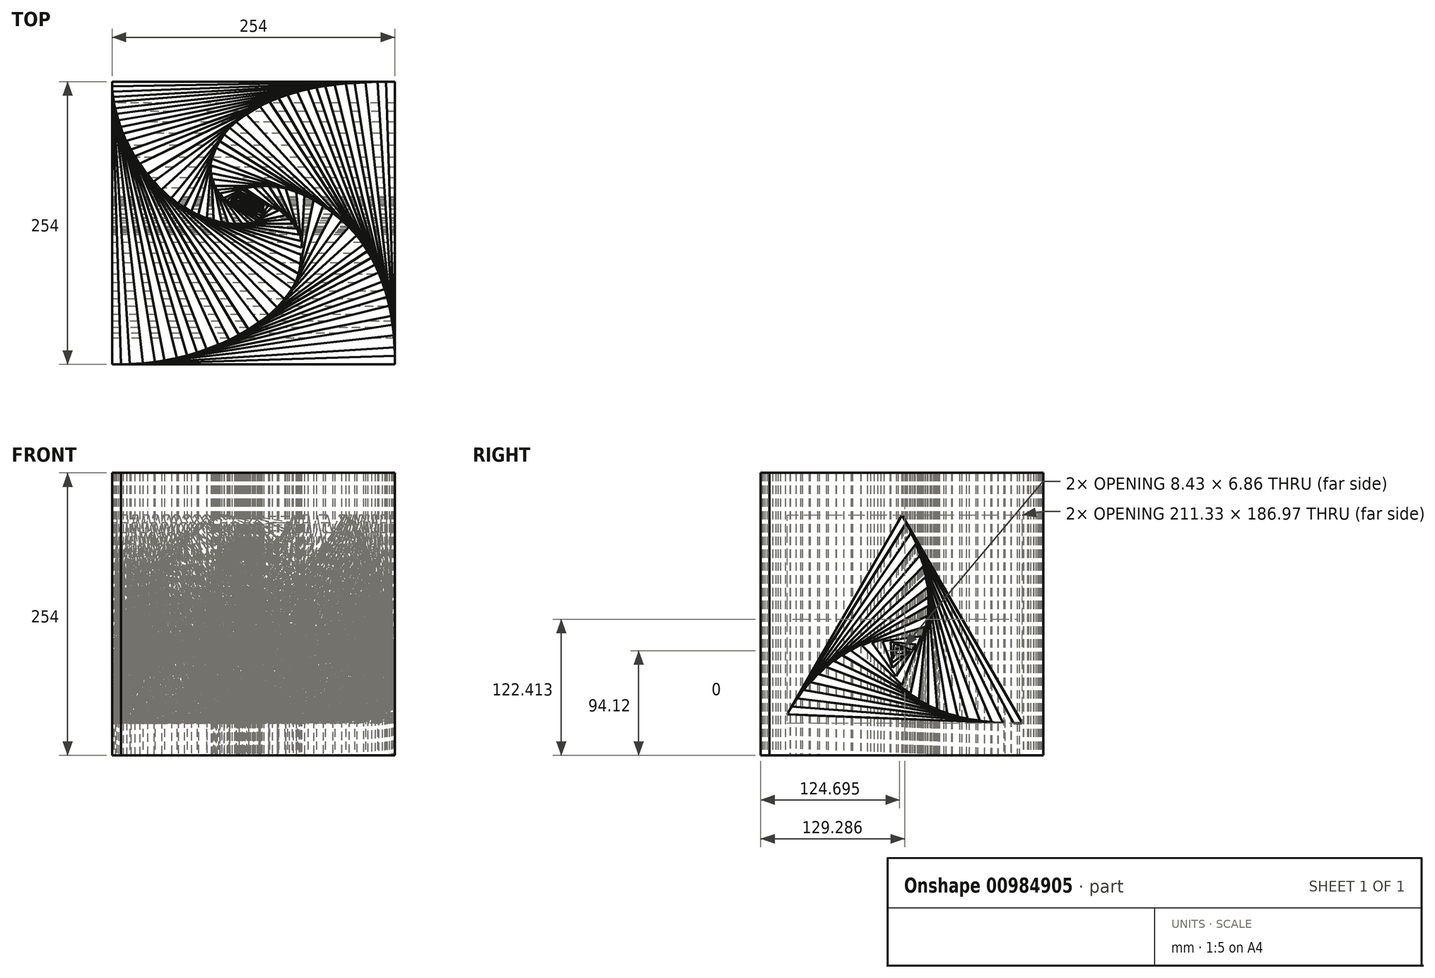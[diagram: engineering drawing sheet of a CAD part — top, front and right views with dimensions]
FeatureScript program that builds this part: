
annotation { "Feature Type Name" : "Feature", "Feature Type Description" : "" }
export const myFeature = defineFeature(function(context is Context, id is Id, definition is map)
    precondition{}
    {
        {
            var Q0;
            Q0=qCreatedBy(makeId("Top.planeOp"),FACE);
            var sketch = newSketch(context, id + "F0", { "sketchPlane" : qUnion([Q0])});
            skLineSegment(sketch, "E0.bottom", {"start": v(-127, 127) * mm, "end": v(127, 127) * mm});
            skLineSegment(sketch, "E0.top", {"start": v(-127, -127) * mm, "end": v(127, -127) * mm});
            skLineSegment(sketch, "E0.left", {"start": v(-127, 127) * mm, "end": v(-127, -127) * mm});
            skLineSegment(sketch, "E0.right", {"start": v(127, 127) * mm, "end": v(127, -127) * mm});
            skPoint(sketch, "E0.middle", {"position": v(0, 0) * mm});
            skLineSegment(sketch, "E1", {"start": v(-127, 127) * mm, "end": v(-119.05, -127) * mm});
            skLineSegment(sketch, "E2", {"start": v(-119.05, -127) * mm, "end": v(127, -119.3) * mm});
            skLineSegment(sketch, "E3", {"start": v(127, -119.3) * mm, "end": v(119.3, 127) * mm});
            skLineSegment(sketch, "E4", {"start": v(119.3, 127) * mm, "end": v(-126.87, 122.79) * mm});
            skLineSegment(sketch, "E5", {"start": v(-126.87, 122.79) * mm, "end": v(-111, -126.75) * mm});
            skLineSegment(sketch, "E6", {"start": v(-111, -126.75) * mm, "end": v(126.76, -111.62) * mm});
            skLineSegment(sketch, "E7", {"start": v(126.76, -111.62) * mm, "end": v(111.59, 126.87) * mm});
            skLineSegment(sketch, "E8", {"start": v(111.59, 126.87) * mm, "end": v(-126.58, 118.23) * mm});
            skLineSegment(sketch, "E9", {"start": v(-126.58, 118.23) * mm, "end": v(-99.33, -126) * mm});
            skLineSegment(sketch, "E10", {"start": v(-99.33, -126) * mm, "end": v(126.07, -100.86) * mm});
            skLineSegment(sketch, "E11", {"start": v(126.07, -100.86) * mm, "end": v(100.71, 126.47) * mm});
            skLineSegment(sketch, "E12", {"start": v(100.71, 126.47) * mm, "end": v(-126.05, 113.53) * mm});
            skLineSegment(sketch, "E13", {"start": v(-126.05, 113.53) * mm, "end": v(-88.65, -124.81) * mm});
            skLineSegment(sketch, "E14", {"start": v(-88.65, -124.81) * mm, "end": v(125, -91.28) * mm});
            skLineSegment(sketch, "E15", {"start": v(125, -91.28) * mm, "end": v(90.92, 125.91) * mm});
            skLineSegment(sketch, "E16", {"start": v(90.92, 125.91) * mm, "end": v(-125.33, 108.92) * mm});
            skLineSegment(sketch, "E17", {"start": v(-125.33, 108.92) * mm, "end": v(-79.79, -123.42) * mm});
            skLineSegment(sketch, "E18", {"start": v(-79.79, -123.42) * mm, "end": v(123.79, -83.52) * mm});
            skLineSegment(sketch, "E19", {"start": v(123.79, -83.52) * mm, "end": v(82.86, 125.28) * mm});
            skLineSegment(sketch, "E20", {"start": v(82.86, 125.28) * mm, "end": v(-124.22, 103.24) * mm});
            skLineSegment(sketch, "E21", {"start": v(-124.22, 103.24) * mm, "end": v(-68.88, -121.29) * mm});
            skLineSegment(sketch, "E22", {"start": v(-68.88, -121.29) * mm, "end": v(121.97, -74.25) * mm});
            skLineSegment(sketch, "E23", {"start": v(121.97, -74.25) * mm, "end": v(73.06, 124.24) * mm});
            skLineSegment(sketch, "E24", {"start": v(73.06, 124.24) * mm, "end": v(-122.95, 98.1) * mm});
            skLineSegment(sketch, "E25", {"start": v(-122.95, 98.1) * mm, "end": v(-59.5, -118.98) * mm});
            skLineSegment(sketch, "E26", {"start": v(-59.5, -118.98) * mm, "end": v(120.06, -66.5) * mm});
            skLineSegment(sketch, "E27", {"start": v(120.06, -66.5) * mm, "end": v(64.65, 123.12) * mm});
            skLineSegment(sketch, "E28", {"start": v(64.65, 123.12) * mm, "end": v(-121.26, 92.3) * mm});
            skLineSegment(sketch, "E29", {"start": v(-121.26, 92.3) * mm, "end": v(-50.64, -116.38) * mm});
            skLineSegment(sketch, "E30", {"start": v(-50.64, -116.38) * mm, "end": v(117.97, -59.33) * mm});
            skLineSegment(sketch, "E31", {"start": v(117.97, -59.33) * mm, "end": v(56.68, 121.8) * mm});
            skLineSegment(sketch, "E32", {"start": v(56.68, 121.8) * mm, "end": v(-119.2, 86.25) * mm});
            skLineSegment(sketch, "E33", {"start": v(-119.2, 86.25) * mm, "end": v(-42.07, -113.48) * mm});
            skLineSegment(sketch, "E34", {"start": v(-42.07, -113.48) * mm, "end": v(115.68, -52.56) * mm});
            skLineSegment(sketch, "E35", {"start": v(115.68, -52.56) * mm, "end": v(48.94, 120.23) * mm});
            skLineSegment(sketch, "E36", {"start": v(48.94, 120.23) * mm, "end": v(-116.98, 80.48) * mm});
            skLineSegment(sketch, "E37", {"start": v(-116.98, 80.48) * mm, "end": v(-31.49, -109.4) * mm});
            skLineSegment(sketch, "E38", {"start": v(-31.49, -109.4) * mm, "end": v(112.58, -44.53) * mm});
            skLineSegment(sketch, "E39", {"start": v(112.58, -44.53) * mm, "end": v(39.42, 117.95) * mm});
            skLineSegment(sketch, "E40", {"start": v(39.42, 117.95) * mm, "end": v(-114.03, 73.93) * mm});
            skLineSegment(sketch, "E41", {"start": v(-114.03, 73.93) * mm, "end": v(-21.72, -105) * mm});
            skLineSegment(sketch, "E42", {"start": v(-21.72, -105) * mm, "end": v(109.35, -37.38) * mm});
            skLineSegment(sketch, "E43", {"start": v(109.35, -37.38) * mm, "end": v(30.54, 115.4) * mm});
            skLineSegment(sketch, "E44", {"start": v(30.54, 115.4) * mm, "end": v(-110.01, 66.14) * mm});
            skLineSegment(sketch, "E45", {"start": v(-110.01, 66.14) * mm, "end": v(-12.99, -100.5) * mm});
            skLineSegment(sketch, "E46", {"start": v(-12.99, -100.5) * mm, "end": v(106.13, -31.13) * mm});
            skLineSegment(sketch, "E47", {"start": v(106.13, -31.13) * mm, "end": v(22.46, 112.57) * mm});
            skLineSegment(sketch, "E48", {"start": v(22.46, 112.57) * mm, "end": v(-106.49, 60.09) * mm});
            skLineSegment(sketch, "E49", {"start": v(-106.49, 60.09) * mm, "end": v(-4.22, -95.4) * mm});
            skLineSegment(sketch, "E50", {"start": v(-4.22, -95.4) * mm, "end": v(102.63, -25.11) * mm});
            skLineSegment(sketch, "E51", {"start": v(102.63, -25.11) * mm, "end": v(14.26, 109.24) * mm});
            skLineSegment(sketch, "E52", {"start": v(14.26, 109.24) * mm, "end": v(-102.15, 53.5) * mm});
            skLineSegment(sketch, "E53", {"start": v(-102.15, 53.5) * mm, "end": v(4.72, -89.5) * mm});
            skLineSegment(sketch, "E54", {"start": v(4.72, -89.5) * mm, "end": v(98.76, -19.23) * mm});
            skLineSegment(sketch, "E55", {"start": v(98.76, -19.23) * mm, "end": v(5.78, 105.18) * mm});
            skLineSegment(sketch, "E56", {"start": v(5.78, 105.18) * mm, "end": v(-95.2, 44.2) * mm});
            skLineSegment(sketch, "E57", {"start": v(-95.2, 44.2) * mm, "end": v(13.74, -82.77) * mm});
            skLineSegment(sketch, "E58", {"start": v(13.74, -82.77) * mm, "end": v(92.63, -11.03) * mm});
            skLineSegment(sketch, "E59", {"start": v(92.63, -11.03) * mm, "end": v(-6.37, 97.84) * mm});
            skLineSegment(sketch, "E60", {"start": v(-6.37, 97.84) * mm, "end": v(-89.35, 37.38) * mm});
            skLineSegment(sketch, "E61", {"start": v(-89.35, 37.38) * mm, "end": v(21.24, -75.94) * mm});
            skLineSegment(sketch, "E62", {"start": v(21.24, -75.94) * mm, "end": v(85.78, -3.5) * mm});
            skLineSegment(sketch, "E63", {"start": v(85.78, -3.5) * mm, "end": v(-15.42, 91.25) * mm});
            skLineSegment(sketch, "E64", {"start": v(-15.42, 91.25) * mm, "end": v(-82.44, 30.3) * mm});
            skLineSegment(sketch, "E65", {"start": v(-82.44, 30.3) * mm, "end": v(28.14, -68.2) * mm});
            skLineSegment(sketch, "E66", {"start": v(28.14, -68.2) * mm, "end": v(79.25, 2.62) * mm});
            skLineSegment(sketch, "E67", {"start": v(79.25, 2.62) * mm, "end": v(-21.42, 85.8) * mm});
            skLineSegment(sketch, "E68", {"start": v(-21.42, 85.8) * mm, "end": v(-73.7, 22.51) * mm});
            skLineSegment(sketch, "E69", {"start": v(-73.7, 22.51) * mm, "end": v(34.67, -59.15) * mm});
            skLineSegment(sketch, "E70", {"start": v(34.67, -59.15) * mm, "end": v(71.24, 9.23) * mm});
            skLineSegment(sketch, "E71", {"start": v(71.24, 9.23) * mm, "end": v(-26.43, 79.72) * mm});
            skLineSegment(sketch, "E72", {"start": v(-26.43, 79.72) * mm, "end": v(-67.61, 17.93) * mm});
            skLineSegment(sketch, "E73", {"start": v(-67.61, 17.93) * mm, "end": v(38.19, -52.58) * mm});
            skLineSegment(sketch, "E74", {"start": v(38.19, -52.58) * mm, "end": v(62.66, 15.43) * mm});
            skLineSegment(sketch, "E75", {"start": v(62.66, 15.43) * mm, "end": v(-30.38, 73.8) * mm});
            skLineSegment(sketch, "E76", {"start": v(-30.38, 73.8) * mm, "end": v(-62.2, 14.31) * mm});
            skLineSegment(sketch, "E77", {"start": v(-62.2, 14.31) * mm, "end": v(40.64, -45.77) * mm});
            skLineSegment(sketch, "E78", {"start": v(40.64, -45.77) * mm, "end": v(53.91, 20.91) * mm});
            skLineSegment(sketch, "E79", {"start": v(53.91, 20.91) * mm, "end": v(-33.63, 67.73) * mm});
            skLineSegment(sketch, "E80", {"start": v(-33.63, 67.73) * mm, "end": v(-55.9, 10.64) * mm});
            skLineSegment(sketch, "E81", {"start": v(-55.9, 10.64) * mm, "end": v(42.4, -36.95) * mm});
            skLineSegment(sketch, "E82", {"start": v(42.4, -36.95) * mm, "end": v(45.79, 25.26) * mm});
            skLineSegment(sketch, "E83", {"start": v(45.79, 25.26) * mm, "end": v(-37.51, 57.77) * mm});
            skLineSegment(sketch, "E84", {"start": v(-37.51, 57.77) * mm, "end": v(-49.59, 7.58) * mm});
            skLineSegment(sketch, "E85", {"start": v(-49.59, 7.58) * mm, "end": v(42.85, -28.5) * mm});
            skLineSegment(sketch, "E86", {"start": v(-37.51, 57.77) * mm, "end": v(-41.95, 4.6) * mm});
            skLineSegment(sketch, "E87", {"start": v(-41.95, 4.6) * mm, "end": v(43.2, -22.06) * mm});
            skLineSegment(sketch, "E88", {"start": v(43.2, -22.06) * mm, "end": v(38.47, 28.12) * mm});
            skLineSegment(sketch, "E89", {"start": v(38.47, 28.12) * mm, "end": v(-38.03, 51.63) * mm});
            skLineSegment(sketch, "E90", {"start": v(-38.03, 51.63) * mm, "end": v(-35.88, 2.7) * mm});
            skLineSegment(sketch, "E91", {"start": v(-35.88, 2.7) * mm, "end": v(42.65, -16.2) * mm});
            skLineSegment(sketch, "E92", {"start": v(42.65, -16.2) * mm, "end": v(29.11, 31) * mm});
            skLineSegment(sketch, "E93", {"start": v(29.11, 31) * mm, "end": v(-37.73, 44.93) * mm});
            skLineSegment(sketch, "E94", {"start": v(-37.73, 44.93) * mm, "end": v(-28.57, 0.94) * mm});
            skLineSegment(sketch, "E95", {"start": v(-28.57, 0.94) * mm, "end": v(40.96, -10.3) * mm});
            skLineSegment(sketch, "E96", {"start": v(40.96, -10.3) * mm, "end": v(21.45, 32.59) * mm});
            skLineSegment(sketch, "E97", {"start": v(21.45, 32.59) * mm, "end": v(-36.55, 39.26) * mm});
            skLineSegment(sketch, "E98", {"start": v(-36.55, 39.26) * mm, "end": v(-22.76, 0) * mm});
            skLineSegment(sketch, "E99", {"start": v(-22.76, 0) * mm, "end": v(38.6, -5.12) * mm});
            skLineSegment(sketch, "E100", {"start": v(38.6, -5.12) * mm, "end": v(13.87, 33.46) * mm});
            skLineSegment(sketch, "E101", {"start": v(13.87, 33.46) * mm, "end": v(-34.51, 33.46) * mm});
            skLineSegment(sketch, "E102", {"start": v(-34.51, 33.46) * mm, "end": v(-16.37, -0.53) * mm});
            skLineSegment(sketch, "E103", {"start": v(-16.37, -0.53) * mm, "end": v(35.66, -0.53) * mm});
            skLineSegment(sketch, "E104", {"start": v(35.66, -0.53) * mm, "end": v(6.5, 33.46) * mm});
            skLineSegment(sketch, "E105", {"start": v(6.5, 33.46) * mm, "end": v(-32.55, 29.77) * mm});
            skLineSegment(sketch, "E106", {"start": v(-32.55, 29.77) * mm, "end": v(-10.06, -0.53) * mm});
            skLineSegment(sketch, "E107", {"start": v(-10.06, -0.53) * mm, "end": v(32.23, 3.46) * mm});
            skLineSegment(sketch, "E108", {"start": v(32.23, 3.46) * mm, "end": v(0, 32.85) * mm});
            skLineSegment(sketch, "E109", {"start": v(0, 32.85) * mm, "end": v(-30.16, 26.56) * mm});
            skLineSegment(sketch, "E110", {"start": v(-30.16, 26.56) * mm, "end": v(-4.43, 0) * mm});
            skLineSegment(sketch, "E111", {"start": v(-4.43, 0) * mm, "end": v(28.5, 6.86) * mm});
            skLineSegment(sketch, "E112", {"start": v(28.5, 6.86) * mm, "end": v(-7.55, 31.28) * mm});
            skPoint(sketch, "E112.endSnap0", {"position": v(-7.55, 35.92) * mm});
            skLineSegment(sketch, "E113", {"start": v(-7.55, 31.28) * mm, "end": v(-26.42, 22.7) * mm});
            skLineSegment(sketch, "E114", {"start": v(-26.42, 22.7) * mm, "end": v(0, 0.92) * mm});
            skLineSegment(sketch, "E115", {"start": v(0, 0.92) * mm, "end": v(22.3, 11.06) * mm});
            skLineSegment(sketch, "E116", {"start": v(22.3, 11.06) * mm, "end": v(-10.15, 30.1) * mm});
            skLineSegment(sketch, "E117", {"start": v(-10.15, 30.1) * mm, "end": v(-23.64, 20.4) * mm});
            skLineSegment(sketch, "E118", {"start": v(-23.64, 20.4) * mm, "end": v(3.33, 2.44) * mm});
            skLineSegment(sketch, "E119", {"start": v(3.33, 2.44) * mm, "end": v(17, 14.17) * mm});
            skLineSegment(sketch, "E120", {"start": v(17, 14.17) * mm, "end": v(-12.61, 28.32) * mm});
            skLineSegment(sketch, "E121", {"start": v(-12.61, 28.32) * mm, "end": v(-21.27, 18.83) * mm});
            skLineSegment(sketch, "E122", {"start": v(-21.27, 18.83) * mm, "end": v(5.65, 4.43) * mm});
            skLineSegment(sketch, "E123", {"start": v(5.65, 4.43) * mm, "end": v(13.32, 15.93) * mm});
            skLineSegment(sketch, "E124", {"start": v(13.32, 15.93) * mm, "end": v(-14.14, 26.65) * mm});
            skLineSegment(sketch, "E125", {"start": v(-14.14, 26.65) * mm, "end": v(-19.33, 17.8) * mm});
            skLineSegment(sketch, "E126", {"start": v(-19.33, 17.8) * mm, "end": v(7.07, 6.56) * mm});
            skLineSegment(sketch, "E127", {"start": v(7.07, 6.56) * mm, "end": v(9.35, 17.48) * mm});
            skLineSegment(sketch, "E128", {"start": v(9.35, 17.48) * mm, "end": v(-15.1, 25) * mm});
            skLineSegment(sketch, "E129", {"start": v(-15.1, 25) * mm, "end": v(-17.07, 16.83) * mm});
            skLineSegment(sketch, "E130", {"start": v(-17.07, 16.83) * mm, "end": v(7.63, 9.24) * mm});
            skLineSegment(sketch, "E131", {"start": v(7.63, 9.24) * mm, "end": v(6.78, 18.27) * mm});
            skLineSegment(sketch, "E132", {"start": v(6.78, 18.27) * mm, "end": v(-15.6, 22.94) * mm});
            skLineSegment(sketch, "E133", {"start": v(-15.6, 22.94) * mm, "end": v(-14.97, 16.18) * mm});
            skLineSegment(sketch, "E134", {"start": v(-14.97, 16.18) * mm, "end": v(7.41, 11.52) * mm});
            skLineSegment(sketch, "E135", {"start": v(7.41, 11.52) * mm, "end": v(4.09, 18.83) * mm});
            skLineSegment(sketch, "E136", {"start": v(4.09, 18.83) * mm, "end": v(-15.37, 20.45) * mm});
            skLineSegment(sketch, "E137", {"start": v(-15.37, 20.45) * mm, "end": v(-13.27, 15.83) * mm});
            skLineSegment(sketch, "E138", {"start": v(-13.27, 15.83) * mm, "end": v(6.49, 13.56) * mm});
            skLineSegment(sketch, "E139", {"start": v(6.49, 13.56) * mm, "end": v(1.8, 19.02) * mm});
            skLineSegment(sketch, "E140", {"start": v(1.8, 19.02) * mm, "end": v(-14.72, 19.02) * mm});
            skLineSegment(sketch, "E141", {"start": v(-14.72, 19.02) * mm, "end": v(-10.92, 15.56) * mm});
            skLineSegment(sketch, "E142", {"start": v(-10.92, 15.56) * mm, "end": v(5.54, 14.66) * mm});
            skLineSegment(sketch, "E143", {"start": v(5.54, 14.66) * mm, "end": v(0.25, 19.02) * mm});
            skLineSegment(sketch, "E144", {"start": v(0.25, 19.02) * mm, "end": v(-13.31, 17.74) * mm});
            skLineSegment(sketch, "E145", {"start": v(-10.92, 15.56) * mm, "end": v(4.45, 15.56) * mm});
            skLineSegment(sketch, "E146", {"start": v(4.45, 15.56) * mm, "end": v(-1.2, 18.89) * mm});
            skLineSegment(sketch, "E147", {"start": v(-1.2, 18.89) * mm, "end": v(-12.62, 17.1) * mm});
            skLineSegment(sketch, "E148", {"start": v(-12.62, 17.1) * mm, "end": v(-10.06, 15.56) * mm});
            skLineSegment(sketch, "E149", {"start": v(-10.06, 15.56) * mm, "end": v(3.1, 16.35) * mm});
            skLineSegment(sketch, "E150", {"start": v(3.1, 16.35) * mm, "end": v(-2.92, 18.62) * mm});
            skLineSegment(sketch, "E151", {"start": v(-2.92, 18.62) * mm, "end": v(-11.74, 16.57) * mm});
            skLineSegment(sketch, "E152", {"start": v(-11.74, 16.57) * mm, "end": v(-9.4, 15.6) * mm});
            skLineSegment(sketch, "E153", {"start": v(-9.4, 15.6) * mm, "end": v(1.73, 16.87) * mm});
            skLineSegment(sketch, "E154", {"start": v(1.73, 16.87) * mm, "end": v(-4.05, 18.36) * mm});
            skLineSegment(sketch, "E155", {"start": v(-4.05, 18.36) * mm, "end": v(-10.92, 16.23) * mm});
            skLineSegment(sketch, "E156", {"start": v(-10.92, 16.23) * mm, "end": v(-8.93, 15.65) * mm});
            skLineSegment(sketch, "E157", {"start": v(-8.93, 15.65) * mm, "end": v(0, 17.31) * mm});
            skLineSegment(sketch, "E158", {"start": v(0, 17.31) * mm, "end": v(-4.78, 18.13) * mm});
            skLineSegment(sketch, "E159", {"start": v(-4.78, 18.13) * mm, "end": v(-9.92, 15.94) * mm});
            skLineSegment(sketch, "E160", {"start": v(-9.92, 15.94) * mm, "end": v(-8.23, 15.78) * mm});
            skLineSegment(sketch, "E161", {"start": v(-8.23, 15.78) * mm, "end": v(-1.2, 17.52) * mm});
            skLineSegment(sketch, "E162", {"start": v(-1.2, 17.52) * mm, "end": v(-5.65, 17.76) * mm});
            skSolve(sketch);
        }
        {
            var Q0;
            {var subQ0=sQuery(id+"F0.wireOp",EDGE,"E0.left");Q0=makeQuery(id+"F0.imprint","IMPRINT",FACE,{"disambiguationData":[TD([[makeQuery(id+"F0.imprint","IMPRINT",EDGE,{"derivedFrom":subQ0}),1.0]])]});}
            var Q1;
            {var subQ0=sQuery(id+"F0.wireOp",EDGE,"E6");var subQ1=sQuery(id+"F0.wireOp",EDGE,"E5");var subQ2=makeQuery(id+"F0.imprint","INTERSECT",VERTEX,{"derivedFrom":[sQuery(id+"F0.wireOp",EDGE,"E2"),subQ1,subQ0]});Q1=makeQuery(id+"F0.imprint","IMPRINT",FACE,{"disambiguationData":[TD([[makeQuery(id+"F0.imprint","IMPRINT",EDGE,{"disambiguationData":[TD([[subQ2,1.0]])],"derivedFrom":subQ1}),1.0]])]});}
            var Q2;
            {var subQ0=sQuery(id+"F0.wireOp",EDGE,"E14");var subQ1=sQuery(id+"F0.wireOp",EDGE,"E13");var subQ2=makeQuery(id+"F0.imprint","INTERSECT",VERTEX,{"derivedFrom":[sQuery(id+"F0.wireOp",EDGE,"E10"),subQ1,subQ0]});Q2=makeQuery(id+"F0.imprint","IMPRINT",FACE,{"disambiguationData":[TD([[makeQuery(id+"F0.imprint","IMPRINT",EDGE,{"disambiguationData":[TD([[subQ2,1.0]])],"derivedFrom":subQ1}),1.0]])]});}
            var Q3;
            {var subQ0=sQuery(id+"F0.wireOp",EDGE,"E22");var subQ1=sQuery(id+"F0.wireOp",EDGE,"E21");var subQ2=makeQuery(id+"F0.imprint","INTERSECT",VERTEX,{"derivedFrom":[sQuery(id+"F0.wireOp",EDGE,"E18"),subQ1,subQ0]});Q3=makeQuery(id+"F0.imprint","IMPRINT",FACE,{"disambiguationData":[TD([[makeQuery(id+"F0.imprint","IMPRINT",EDGE,{"disambiguationData":[TD([[subQ2,1.0]])],"derivedFrom":subQ1}),1.0]])]});}
            var Q4;
            {var subQ0=sQuery(id+"F0.wireOp",EDGE,"E30");var subQ1=sQuery(id+"F0.wireOp",EDGE,"E29");var subQ2=makeQuery(id+"F0.imprint","INTERSECT",VERTEX,{"derivedFrom":[sQuery(id+"F0.wireOp",EDGE,"E26"),subQ1,subQ0]});Q4=makeQuery(id+"F0.imprint","IMPRINT",FACE,{"disambiguationData":[TD([[makeQuery(id+"F0.imprint","IMPRINT",EDGE,{"disambiguationData":[TD([[subQ2,1.0]])],"derivedFrom":subQ1}),1.0]])]});}
            var Q5;
            {var subQ0=sQuery(id+"F0.wireOp",EDGE,"E38");var subQ1=sQuery(id+"F0.wireOp",EDGE,"E37");var subQ2=makeQuery(id+"F0.imprint","INTERSECT",VERTEX,{"derivedFrom":[sQuery(id+"F0.wireOp",EDGE,"E34"),subQ1,subQ0]});Q5=makeQuery(id+"F0.imprint","IMPRINT",FACE,{"disambiguationData":[TD([[makeQuery(id+"F0.imprint","IMPRINT",EDGE,{"disambiguationData":[TD([[subQ2,1.0]])],"derivedFrom":subQ1}),1.0]])]});}
            var Q6;
            {var subQ0=sQuery(id+"F0.wireOp",EDGE,"E46");var subQ1=sQuery(id+"F0.wireOp",EDGE,"E45");var subQ2=makeQuery(id+"F0.imprint","INTERSECT",VERTEX,{"derivedFrom":[sQuery(id+"F0.wireOp",EDGE,"E42"),subQ1,subQ0]});Q6=makeQuery(id+"F0.imprint","IMPRINT",FACE,{"disambiguationData":[TD([[makeQuery(id+"F0.imprint","IMPRINT",EDGE,{"disambiguationData":[TD([[subQ2,1.0]])],"derivedFrom":subQ1}),1.0]])]});}
            var Q7;
            {var subQ0=sQuery(id+"F0.wireOp",EDGE,"E54");var subQ1=sQuery(id+"F0.wireOp",EDGE,"E53");var subQ2=makeQuery(id+"F0.imprint","INTERSECT",VERTEX,{"derivedFrom":[sQuery(id+"F0.wireOp",EDGE,"E50"),subQ1,subQ0]});Q7=makeQuery(id+"F0.imprint","IMPRINT",FACE,{"disambiguationData":[TD([[makeQuery(id+"F0.imprint","IMPRINT",EDGE,{"disambiguationData":[TD([[subQ2,1.0]])],"derivedFrom":subQ1}),1.0]])]});}
            var Q8;
            {var subQ0=sQuery(id+"F0.wireOp",EDGE,"E62");var subQ1=sQuery(id+"F0.wireOp",EDGE,"E61");var subQ2=makeQuery(id+"F0.imprint","INTERSECT",VERTEX,{"derivedFrom":[sQuery(id+"F0.wireOp",EDGE,"E58"),subQ1,subQ0]});Q8=makeQuery(id+"F0.imprint","IMPRINT",FACE,{"disambiguationData":[TD([[makeQuery(id+"F0.imprint","IMPRINT",EDGE,{"disambiguationData":[TD([[subQ2,1.0]])],"derivedFrom":subQ1}),1.0]])]});}
            var Q9;
            {var subQ0=sQuery(id+"F0.wireOp",EDGE,"E70");var subQ1=sQuery(id+"F0.wireOp",EDGE,"E69");var subQ2=makeQuery(id+"F0.imprint","INTERSECT",VERTEX,{"derivedFrom":[sQuery(id+"F0.wireOp",EDGE,"E66"),subQ1,subQ0]});Q9=makeQuery(id+"F0.imprint","IMPRINT",FACE,{"disambiguationData":[TD([[makeQuery(id+"F0.imprint","IMPRINT",EDGE,{"disambiguationData":[TD([[subQ2,1.0]])],"derivedFrom":subQ1}),1.0]])]});}
            var Q10;
            {var subQ0=sQuery(id+"F0.wireOp",EDGE,"E78");var subQ1=sQuery(id+"F0.wireOp",EDGE,"E77");var subQ2=makeQuery(id+"F0.imprint","INTERSECT",VERTEX,{"derivedFrom":[sQuery(id+"F0.wireOp",EDGE,"E74"),subQ1,subQ0]});Q10=makeQuery(id+"F0.imprint","IMPRINT",FACE,{"disambiguationData":[TD([[makeQuery(id+"F0.imprint","IMPRINT",EDGE,{"disambiguationData":[TD([[subQ2,1.0]])],"derivedFrom":subQ1}),1.0]])]});}
            var Q11;
            {var subQ0=sQuery(id+"F0.wireOp",EDGE,"E85");var subQ1=sQuery(id+"F0.wireOp",EDGE,"E82");var subQ2=makeQuery(id+"F0.imprint","INTERSECT",VERTEX,{"derivedFrom":[subQ1,subQ0]});Q11=makeQuery(id+"F0.imprint","IMPRINT",FACE,{"disambiguationData":[TD([[makeQuery(id+"F0.imprint","IMPRINT",EDGE,{"disambiguationData":[TD([[subQ2,-1.0]])],"derivedFrom":subQ1}),1.0]])]});}
            var Q12;
            {var subQ0=sQuery(id+"F0.wireOp",EDGE,"E92");var subQ1=sQuery(id+"F0.wireOp",EDGE,"E91");var subQ2=makeQuery(id+"F0.imprint","INTERSECT",VERTEX,{"derivedFrom":[sQuery(id+"F0.wireOp",EDGE,"E88"),subQ1,subQ0]});Q12=makeQuery(id+"F0.imprint","IMPRINT",FACE,{"disambiguationData":[TD([[makeQuery(id+"F0.imprint","IMPRINT",EDGE,{"disambiguationData":[TD([[subQ2,1.0]])],"derivedFrom":subQ1}),1.0]])]});}
            var Q13;
            {var subQ0=sQuery(id+"F0.wireOp",EDGE,"E100");var subQ1=sQuery(id+"F0.wireOp",EDGE,"E99");var subQ2=makeQuery(id+"F0.imprint","INTERSECT",VERTEX,{"derivedFrom":[sQuery(id+"F0.wireOp",EDGE,"E96"),subQ1,subQ0]});Q13=makeQuery(id+"F0.imprint","IMPRINT",FACE,{"disambiguationData":[TD([[makeQuery(id+"F0.imprint","IMPRINT",EDGE,{"disambiguationData":[TD([[subQ2,1.0]])],"derivedFrom":subQ1}),1.0]])]});}
            var Q14;
            {var subQ0=sQuery(id+"F0.wireOp",EDGE,"E108");var subQ1=sQuery(id+"F0.wireOp",EDGE,"E107");var subQ2=makeQuery(id+"F0.imprint","INTERSECT",VERTEX,{"derivedFrom":[sQuery(id+"F0.wireOp",EDGE,"E104"),subQ1,subQ0]});Q14=makeQuery(id+"F0.imprint","IMPRINT",FACE,{"disambiguationData":[TD([[makeQuery(id+"F0.imprint","IMPRINT",EDGE,{"disambiguationData":[TD([[subQ2,1.0]])],"derivedFrom":subQ1}),1.0]])]});}
            var Q15;
            {var subQ0=sQuery(id+"F0.wireOp",EDGE,"E116");var subQ1=sQuery(id+"F0.wireOp",EDGE,"E115");var subQ2=makeQuery(id+"F0.imprint","INTERSECT",VERTEX,{"derivedFrom":[sQuery(id+"F0.wireOp",EDGE,"E112"),subQ1,subQ0]});Q15=makeQuery(id+"F0.imprint","IMPRINT",FACE,{"disambiguationData":[TD([[makeQuery(id+"F0.imprint","IMPRINT",EDGE,{"disambiguationData":[TD([[subQ2,1.0]])],"derivedFrom":subQ1}),1.0]])]});}
            var Q16;
            {var subQ0=sQuery(id+"F0.wireOp",EDGE,"E124");var subQ1=sQuery(id+"F0.wireOp",EDGE,"E123");var subQ2=makeQuery(id+"F0.imprint","INTERSECT",VERTEX,{"derivedFrom":[sQuery(id+"F0.wireOp",EDGE,"E120"),subQ1,subQ0]});Q16=makeQuery(id+"F0.imprint","IMPRINT",FACE,{"disambiguationData":[TD([[makeQuery(id+"F0.imprint","IMPRINT",EDGE,{"disambiguationData":[TD([[subQ2,1.0]])],"derivedFrom":subQ1}),1.0]])]});}
            var Q17;
            {var subQ0=sQuery(id+"F0.wireOp",EDGE,"E132");var subQ1=sQuery(id+"F0.wireOp",EDGE,"E131");var subQ2=makeQuery(id+"F0.imprint","INTERSECT",VERTEX,{"derivedFrom":[sQuery(id+"F0.wireOp",EDGE,"E128"),subQ1,subQ0]});Q17=makeQuery(id+"F0.imprint","IMPRINT",FACE,{"disambiguationData":[TD([[makeQuery(id+"F0.imprint","IMPRINT",EDGE,{"disambiguationData":[TD([[subQ2,1.0]])],"derivedFrom":subQ1}),1.0]])]});}
            var Q18;
            {var subQ0=sQuery(id+"F0.wireOp",EDGE,"E140");var subQ1=sQuery(id+"F0.wireOp",EDGE,"E139");var subQ2=makeQuery(id+"F0.imprint","INTERSECT",VERTEX,{"derivedFrom":[sQuery(id+"F0.wireOp",EDGE,"E136"),subQ1,subQ0]});Q18=makeQuery(id+"F0.imprint","IMPRINT",FACE,{"disambiguationData":[TD([[makeQuery(id+"F0.imprint","IMPRINT",EDGE,{"disambiguationData":[TD([[subQ2,1.0]])],"derivedFrom":subQ1}),1.0]])]});}
            var Q19;
            {var subQ0=sQuery(id+"F0.wireOp",EDGE,"E147");var subQ1=sQuery(id+"F0.wireOp",EDGE,"E146");var subQ2=makeQuery(id+"F0.imprint","INTERSECT",VERTEX,{"derivedFrom":[sQuery(id+"F0.wireOp",EDGE,"E144"),subQ1,subQ0]});Q19=makeQuery(id+"F0.imprint","IMPRINT",FACE,{"disambiguationData":[TD([[makeQuery(id+"F0.imprint","IMPRINT",EDGE,{"disambiguationData":[TD([[subQ2,1.0]])],"derivedFrom":subQ1}),1.0]])]});}
            var Q20;
            {var subQ0=sQuery(id+"F0.wireOp",EDGE,"E155");var subQ1=sQuery(id+"F0.wireOp",EDGE,"E154");var subQ2=makeQuery(id+"F0.imprint","INTERSECT",VERTEX,{"derivedFrom":[sQuery(id+"F0.wireOp",EDGE,"E151"),subQ1,subQ0]});Q20=makeQuery(id+"F0.imprint","IMPRINT",FACE,{"disambiguationData":[TD([[makeQuery(id+"F0.imprint","IMPRINT",EDGE,{"disambiguationData":[TD([[subQ2,1.0]])],"derivedFrom":subQ1}),1.0]])]});}
            var Q21;
            {var subQ0=sQuery(id+"F0.wireOp",EDGE,"E0.right");var subQ1=sQuery(id+"F0.wireOp",EDGE,"E0.top");var subQ2=makeQuery(id+"F0.imprint","INTERSECT",VERTEX,{"derivedFrom":[subQ1,subQ0]});Q21=makeQuery(id+"F0.imprint","IMPRINT",FACE,{"disambiguationData":[TD([[makeQuery(id+"F0.imprint","IMPRINT",EDGE,{"disambiguationData":[TD([[subQ2,1.0]])],"derivedFrom":subQ1}),1.0]])]});}
            var Q22;
            {var subQ0=sQuery(id+"F0.wireOp",EDGE,"E7");var subQ1=sQuery(id+"F0.wireOp",EDGE,"E6");var subQ2=makeQuery(id+"F0.imprint","INTERSECT",VERTEX,{"derivedFrom":[sQuery(id+"F0.wireOp",EDGE,"E3"),subQ1,subQ0]});Q22=makeQuery(id+"F0.imprint","IMPRINT",FACE,{"disambiguationData":[TD([[makeQuery(id+"F0.imprint","IMPRINT",EDGE,{"disambiguationData":[TD([[subQ2,1.0]])],"derivedFrom":subQ1}),1.0]])]});}
            var Q23;
            {var subQ0=sQuery(id+"F0.wireOp",EDGE,"E15");var subQ1=sQuery(id+"F0.wireOp",EDGE,"E14");var subQ2=makeQuery(id+"F0.imprint","INTERSECT",VERTEX,{"derivedFrom":[sQuery(id+"F0.wireOp",EDGE,"E11"),subQ1,subQ0]});Q23=makeQuery(id+"F0.imprint","IMPRINT",FACE,{"disambiguationData":[TD([[makeQuery(id+"F0.imprint","IMPRINT",EDGE,{"disambiguationData":[TD([[subQ2,1.0]])],"derivedFrom":subQ1}),1.0]])]});}
            var Q24;
            {var subQ0=sQuery(id+"F0.wireOp",EDGE,"E23");var subQ1=sQuery(id+"F0.wireOp",EDGE,"E22");var subQ2=makeQuery(id+"F0.imprint","INTERSECT",VERTEX,{"derivedFrom":[sQuery(id+"F0.wireOp",EDGE,"E19"),subQ1,subQ0]});Q24=makeQuery(id+"F0.imprint","IMPRINT",FACE,{"disambiguationData":[TD([[makeQuery(id+"F0.imprint","IMPRINT",EDGE,{"disambiguationData":[TD([[subQ2,1.0]])],"derivedFrom":subQ1}),1.0]])]});}
            var Q25;
            {var subQ0=sQuery(id+"F0.wireOp",EDGE,"E31");var subQ1=sQuery(id+"F0.wireOp",EDGE,"E30");var subQ2=makeQuery(id+"F0.imprint","INTERSECT",VERTEX,{"derivedFrom":[sQuery(id+"F0.wireOp",EDGE,"E27"),subQ1,subQ0]});Q25=makeQuery(id+"F0.imprint","IMPRINT",FACE,{"disambiguationData":[TD([[makeQuery(id+"F0.imprint","IMPRINT",EDGE,{"disambiguationData":[TD([[subQ2,1.0]])],"derivedFrom":subQ1}),1.0]])]});}
            var Q26;
            {var subQ0=sQuery(id+"F0.wireOp",EDGE,"E39");var subQ1=sQuery(id+"F0.wireOp",EDGE,"E38");var subQ2=makeQuery(id+"F0.imprint","INTERSECT",VERTEX,{"derivedFrom":[sQuery(id+"F0.wireOp",EDGE,"E35"),subQ1,subQ0]});Q26=makeQuery(id+"F0.imprint","IMPRINT",FACE,{"disambiguationData":[TD([[makeQuery(id+"F0.imprint","IMPRINT",EDGE,{"disambiguationData":[TD([[subQ2,1.0]])],"derivedFrom":subQ1}),1.0]])]});}
            var Q27;
            {var subQ0=sQuery(id+"F0.wireOp",EDGE,"E47");var subQ1=sQuery(id+"F0.wireOp",EDGE,"E46");var subQ2=makeQuery(id+"F0.imprint","INTERSECT",VERTEX,{"derivedFrom":[sQuery(id+"F0.wireOp",EDGE,"E43"),subQ1,subQ0]});Q27=makeQuery(id+"F0.imprint","IMPRINT",FACE,{"disambiguationData":[TD([[makeQuery(id+"F0.imprint","IMPRINT",EDGE,{"disambiguationData":[TD([[subQ2,1.0]])],"derivedFrom":subQ1}),1.0]])]});}
            var Q28;
            {var subQ0=sQuery(id+"F0.wireOp",EDGE,"E55");var subQ1=sQuery(id+"F0.wireOp",EDGE,"E54");var subQ2=makeQuery(id+"F0.imprint","INTERSECT",VERTEX,{"derivedFrom":[sQuery(id+"F0.wireOp",EDGE,"E51"),subQ1,subQ0]});Q28=makeQuery(id+"F0.imprint","IMPRINT",FACE,{"disambiguationData":[TD([[makeQuery(id+"F0.imprint","IMPRINT",EDGE,{"disambiguationData":[TD([[subQ2,1.0]])],"derivedFrom":subQ1}),1.0]])]});}
            var Q29;
            {var subQ0=sQuery(id+"F0.wireOp",EDGE,"E63");var subQ1=sQuery(id+"F0.wireOp",EDGE,"E62");var subQ2=makeQuery(id+"F0.imprint","INTERSECT",VERTEX,{"derivedFrom":[sQuery(id+"F0.wireOp",EDGE,"E59"),subQ1,subQ0]});Q29=makeQuery(id+"F0.imprint","IMPRINT",FACE,{"disambiguationData":[TD([[makeQuery(id+"F0.imprint","IMPRINT",EDGE,{"disambiguationData":[TD([[subQ2,1.0]])],"derivedFrom":subQ1}),1.0]])]});}
            var Q30;
            {var subQ0=sQuery(id+"F0.wireOp",EDGE,"E71");var subQ1=sQuery(id+"F0.wireOp",EDGE,"E70");var subQ2=makeQuery(id+"F0.imprint","INTERSECT",VERTEX,{"derivedFrom":[sQuery(id+"F0.wireOp",EDGE,"E67"),subQ1,subQ0]});Q30=makeQuery(id+"F0.imprint","IMPRINT",FACE,{"disambiguationData":[TD([[makeQuery(id+"F0.imprint","IMPRINT",EDGE,{"disambiguationData":[TD([[subQ2,1.0]])],"derivedFrom":subQ1}),1.0]])]});}
            var Q31;
            {var subQ0=sQuery(id+"F0.wireOp",EDGE,"E82");var subQ1=makeQuery(id+"F0.imprint","INTERSECT",VERTEX,{"derivedFrom":[subQ0,sQuery(id+"F0.wireOp",EDGE,"E85")]});Q31=makeQuery(id+"F0.imprint","IMPRINT",FACE,{"disambiguationData":[TD([[makeQuery(id+"F0.imprint","IMPRINT",EDGE,{"disambiguationData":[TD([[subQ1,1.0]])],"derivedFrom":subQ0}),-1.0]])]});}
            var Q32;
            {var subQ0=sQuery(id+"F0.wireOp",EDGE,"E89");var subQ1=sQuery(id+"F0.wireOp",EDGE,"E88");var subQ2=makeQuery(id+"F0.imprint","INTERSECT",VERTEX,{"derivedFrom":[sQuery(id+"F0.wireOp",EDGE,"E83"),subQ1,subQ0]});Q32=makeQuery(id+"F0.imprint","IMPRINT",FACE,{"disambiguationData":[TD([[makeQuery(id+"F0.imprint","IMPRINT",EDGE,{"disambiguationData":[TD([[subQ2,1.0]])],"derivedFrom":subQ1}),1.0]])]});}
            var Q33;
            {var subQ0=sQuery(id+"F0.wireOp",EDGE,"E97");var subQ1=sQuery(id+"F0.wireOp",EDGE,"E96");var subQ2=makeQuery(id+"F0.imprint","INTERSECT",VERTEX,{"derivedFrom":[sQuery(id+"F0.wireOp",EDGE,"E93"),subQ1,subQ0]});Q33=makeQuery(id+"F0.imprint","IMPRINT",FACE,{"disambiguationData":[TD([[makeQuery(id+"F0.imprint","IMPRINT",EDGE,{"disambiguationData":[TD([[subQ2,1.0]])],"derivedFrom":subQ1}),1.0]])]});}
            var Q34;
            {var subQ0=sQuery(id+"F0.wireOp",EDGE,"E105");var subQ1=sQuery(id+"F0.wireOp",EDGE,"E104");var subQ2=makeQuery(id+"F0.imprint","INTERSECT",VERTEX,{"derivedFrom":[sQuery(id+"F0.wireOp",EDGE,"E101"),subQ1,subQ0]});Q34=makeQuery(id+"F0.imprint","IMPRINT",FACE,{"disambiguationData":[TD([[makeQuery(id+"F0.imprint","IMPRINT",EDGE,{"disambiguationData":[TD([[subQ2,1.0]])],"derivedFrom":subQ1}),1.0]])]});}
            var Q35;
            {var subQ0=sQuery(id+"F0.wireOp",EDGE,"E113");var subQ1=sQuery(id+"F0.wireOp",EDGE,"E112");var subQ2=makeQuery(id+"F0.imprint","INTERSECT",VERTEX,{"derivedFrom":[sQuery(id+"F0.wireOp",EDGE,"E109"),subQ1,subQ0]});Q35=makeQuery(id+"F0.imprint","IMPRINT",FACE,{"disambiguationData":[TD([[makeQuery(id+"F0.imprint","IMPRINT",EDGE,{"disambiguationData":[TD([[subQ2,1.0]])],"derivedFrom":subQ1}),1.0]])]});}
            var Q36;
            {var subQ0=sQuery(id+"F0.wireOp",EDGE,"E121");var subQ1=sQuery(id+"F0.wireOp",EDGE,"E120");var subQ2=makeQuery(id+"F0.imprint","INTERSECT",VERTEX,{"derivedFrom":[sQuery(id+"F0.wireOp",EDGE,"E117"),subQ1,subQ0]});Q36=makeQuery(id+"F0.imprint","IMPRINT",FACE,{"disambiguationData":[TD([[makeQuery(id+"F0.imprint","IMPRINT",EDGE,{"disambiguationData":[TD([[subQ2,1.0]])],"derivedFrom":subQ1}),1.0]])]});}
            var Q37;
            {var subQ0=sQuery(id+"F0.wireOp",EDGE,"E129");var subQ1=sQuery(id+"F0.wireOp",EDGE,"E128");var subQ2=makeQuery(id+"F0.imprint","INTERSECT",VERTEX,{"derivedFrom":[sQuery(id+"F0.wireOp",EDGE,"E125"),subQ1,subQ0]});Q37=makeQuery(id+"F0.imprint","IMPRINT",FACE,{"disambiguationData":[TD([[makeQuery(id+"F0.imprint","IMPRINT",EDGE,{"disambiguationData":[TD([[subQ2,1.0]])],"derivedFrom":subQ1}),1.0]])]});}
            var Q38;
            {var subQ0=sQuery(id+"F0.wireOp",EDGE,"E137");var subQ1=sQuery(id+"F0.wireOp",EDGE,"E136");var subQ2=makeQuery(id+"F0.imprint","INTERSECT",VERTEX,{"derivedFrom":[sQuery(id+"F0.wireOp",EDGE,"E133"),subQ1,subQ0]});Q38=makeQuery(id+"F0.imprint","IMPRINT",FACE,{"disambiguationData":[TD([[makeQuery(id+"F0.imprint","IMPRINT",EDGE,{"disambiguationData":[TD([[subQ2,1.0]])],"derivedFrom":subQ1}),1.0]])]});}
            var Q39;
            {var subQ0=sQuery(id+"F0.wireOp",EDGE,"E144");var subQ1=sQuery(id+"F0.wireOp",EDGE,"E141");var subQ2=makeQuery(id+"F0.imprint","INTERSECT",VERTEX,{"derivedFrom":[subQ1,subQ0]});Q39=makeQuery(id+"F0.imprint","IMPRINT",FACE,{"disambiguationData":[TD([[makeQuery(id+"F0.imprint","IMPRINT",EDGE,{"disambiguationData":[TD([[subQ2,-1.0]])],"derivedFrom":subQ1}),1.0]])]});}
            var Q40;
            {var subQ0=sQuery(id+"F0.wireOp",EDGE,"E152");var subQ1=sQuery(id+"F0.wireOp",EDGE,"E151");var subQ2=makeQuery(id+"F0.imprint","INTERSECT",VERTEX,{"derivedFrom":[sQuery(id+"F0.wireOp",EDGE,"E148"),subQ1,subQ0]});Q40=makeQuery(id+"F0.imprint","IMPRINT",FACE,{"disambiguationData":[TD([[makeQuery(id+"F0.imprint","IMPRINT",EDGE,{"disambiguationData":[TD([[subQ2,1.0]])],"derivedFrom":subQ1}),1.0]])]});}
            var Q41;
            {var subQ0=sQuery(id+"F0.wireOp",EDGE,"E160");Q41=makeQuery(id+"F0.imprint","IMPRINT",FACE,{"disambiguationData":[TD([[makeQuery(id+"F0.imprint","IMPRINT",EDGE,{"derivedFrom":subQ0}),1.0]])]});}
            var Q42;
            {var subQ0=sQuery(id+"F0.wireOp",EDGE,"E0.right");var subQ1=sQuery(id+"F0.wireOp",EDGE,"E0.bottom");var subQ2=makeQuery(id+"F0.imprint","INTERSECT",VERTEX,{"derivedFrom":[subQ1,subQ0]});Q42=makeQuery(id+"F0.imprint","IMPRINT",FACE,{"disambiguationData":[TD([[makeQuery(id+"F0.imprint","IMPRINT",EDGE,{"disambiguationData":[TD([[subQ2,1.0]])],"derivedFrom":subQ1}),-1.0]])]});}
            var Q43;
            {var subQ0=sQuery(id+"F0.wireOp",EDGE,"E8");var subQ1=sQuery(id+"F0.wireOp",EDGE,"E7");var subQ2=makeQuery(id+"F0.imprint","INTERSECT",VERTEX,{"derivedFrom":[sQuery(id+"F0.wireOp",EDGE,"E4"),subQ1,subQ0]});Q43=makeQuery(id+"F0.imprint","IMPRINT",FACE,{"disambiguationData":[TD([[makeQuery(id+"F0.imprint","IMPRINT",EDGE,{"disambiguationData":[TD([[subQ2,1.0]])],"derivedFrom":subQ1}),1.0]])]});}
            var Q44;
            {var subQ0=sQuery(id+"F0.wireOp",EDGE,"E16");var subQ1=sQuery(id+"F0.wireOp",EDGE,"E15");var subQ2=makeQuery(id+"F0.imprint","INTERSECT",VERTEX,{"derivedFrom":[sQuery(id+"F0.wireOp",EDGE,"E12"),subQ1,subQ0]});Q44=makeQuery(id+"F0.imprint","IMPRINT",FACE,{"disambiguationData":[TD([[makeQuery(id+"F0.imprint","IMPRINT",EDGE,{"disambiguationData":[TD([[subQ2,1.0]])],"derivedFrom":subQ1}),1.0]])]});}
            var Q45;
            {var subQ0=sQuery(id+"F0.wireOp",EDGE,"E24");var subQ1=sQuery(id+"F0.wireOp",EDGE,"E23");var subQ2=makeQuery(id+"F0.imprint","INTERSECT",VERTEX,{"derivedFrom":[sQuery(id+"F0.wireOp",EDGE,"E20"),subQ1,subQ0]});Q45=makeQuery(id+"F0.imprint","IMPRINT",FACE,{"disambiguationData":[TD([[makeQuery(id+"F0.imprint","IMPRINT",EDGE,{"disambiguationData":[TD([[subQ2,1.0]])],"derivedFrom":subQ1}),1.0]])]});}
            var Q46;
            {var subQ0=sQuery(id+"F0.wireOp",EDGE,"E32");var subQ1=sQuery(id+"F0.wireOp",EDGE,"E31");var subQ2=makeQuery(id+"F0.imprint","INTERSECT",VERTEX,{"derivedFrom":[sQuery(id+"F0.wireOp",EDGE,"E28"),subQ1,subQ0]});Q46=makeQuery(id+"F0.imprint","IMPRINT",FACE,{"disambiguationData":[TD([[makeQuery(id+"F0.imprint","IMPRINT",EDGE,{"disambiguationData":[TD([[subQ2,1.0]])],"derivedFrom":subQ1}),1.0]])]});}
            var Q47;
            {var subQ0=sQuery(id+"F0.wireOp",EDGE,"E40");var subQ1=sQuery(id+"F0.wireOp",EDGE,"E39");var subQ2=makeQuery(id+"F0.imprint","INTERSECT",VERTEX,{"derivedFrom":[sQuery(id+"F0.wireOp",EDGE,"E36"),subQ1,subQ0]});Q47=makeQuery(id+"F0.imprint","IMPRINT",FACE,{"disambiguationData":[TD([[makeQuery(id+"F0.imprint","IMPRINT",EDGE,{"disambiguationData":[TD([[subQ2,1.0]])],"derivedFrom":subQ1}),1.0]])]});}
            var Q48;
            {var subQ0=sQuery(id+"F0.wireOp",EDGE,"E48");var subQ1=sQuery(id+"F0.wireOp",EDGE,"E47");var subQ2=makeQuery(id+"F0.imprint","INTERSECT",VERTEX,{"derivedFrom":[sQuery(id+"F0.wireOp",EDGE,"E44"),subQ1,subQ0]});Q48=makeQuery(id+"F0.imprint","IMPRINT",FACE,{"disambiguationData":[TD([[makeQuery(id+"F0.imprint","IMPRINT",EDGE,{"disambiguationData":[TD([[subQ2,1.0]])],"derivedFrom":subQ1}),1.0]])]});}
            var Q49;
            {var subQ0=sQuery(id+"F0.wireOp",EDGE,"E56");var subQ1=sQuery(id+"F0.wireOp",EDGE,"E55");var subQ2=makeQuery(id+"F0.imprint","INTERSECT",VERTEX,{"derivedFrom":[sQuery(id+"F0.wireOp",EDGE,"E52"),subQ1,subQ0]});Q49=makeQuery(id+"F0.imprint","IMPRINT",FACE,{"disambiguationData":[TD([[makeQuery(id+"F0.imprint","IMPRINT",EDGE,{"disambiguationData":[TD([[subQ2,1.0]])],"derivedFrom":subQ1}),1.0]])]});}
            var Q50;
            {var subQ0=sQuery(id+"F0.wireOp",EDGE,"E64");var subQ1=sQuery(id+"F0.wireOp",EDGE,"E63");var subQ2=makeQuery(id+"F0.imprint","INTERSECT",VERTEX,{"derivedFrom":[sQuery(id+"F0.wireOp",EDGE,"E60"),subQ1,subQ0]});Q50=makeQuery(id+"F0.imprint","IMPRINT",FACE,{"disambiguationData":[TD([[makeQuery(id+"F0.imprint","IMPRINT",EDGE,{"disambiguationData":[TD([[subQ2,1.0]])],"derivedFrom":subQ1}),1.0]])]});}
            var Q51;
            {var subQ0=sQuery(id+"F0.wireOp",EDGE,"E72");var subQ1=sQuery(id+"F0.wireOp",EDGE,"E71");var subQ2=makeQuery(id+"F0.imprint","INTERSECT",VERTEX,{"derivedFrom":[sQuery(id+"F0.wireOp",EDGE,"E68"),subQ1,subQ0]});Q51=makeQuery(id+"F0.imprint","IMPRINT",FACE,{"disambiguationData":[TD([[makeQuery(id+"F0.imprint","IMPRINT",EDGE,{"disambiguationData":[TD([[subQ2,1.0]])],"derivedFrom":subQ1}),1.0]])]});}
            var Q52;
            {var subQ0=sQuery(id+"F0.wireOp",EDGE,"E80");var subQ1=sQuery(id+"F0.wireOp",EDGE,"E79");var subQ2=makeQuery(id+"F0.imprint","INTERSECT",VERTEX,{"derivedFrom":[sQuery(id+"F0.wireOp",EDGE,"E76"),subQ1,subQ0]});Q52=makeQuery(id+"F0.imprint","IMPRINT",FACE,{"disambiguationData":[TD([[makeQuery(id+"F0.imprint","IMPRINT",EDGE,{"disambiguationData":[TD([[subQ2,1.0]])],"derivedFrom":subQ1}),1.0]])]});}
            var Q53;
            {var subQ0=sQuery(id+"F0.wireOp",EDGE,"E90");var subQ1=sQuery(id+"F0.wireOp",EDGE,"E89");var subQ2=makeQuery(id+"F0.imprint","INTERSECT",VERTEX,{"derivedFrom":[sQuery(id+"F0.wireOp",EDGE,"E86"),subQ1,subQ0]});Q53=makeQuery(id+"F0.imprint","IMPRINT",FACE,{"disambiguationData":[TD([[makeQuery(id+"F0.imprint","IMPRINT",EDGE,{"disambiguationData":[TD([[subQ2,1.0]])],"derivedFrom":subQ1}),1.0]])]});}
            var Q54;
            {var subQ0=sQuery(id+"F0.wireOp",EDGE,"E98");var subQ1=sQuery(id+"F0.wireOp",EDGE,"E97");var subQ2=makeQuery(id+"F0.imprint","INTERSECT",VERTEX,{"derivedFrom":[sQuery(id+"F0.wireOp",EDGE,"E94"),subQ1,subQ0]});Q54=makeQuery(id+"F0.imprint","IMPRINT",FACE,{"disambiguationData":[TD([[makeQuery(id+"F0.imprint","IMPRINT",EDGE,{"disambiguationData":[TD([[subQ2,1.0]])],"derivedFrom":subQ1}),1.0]])]});}
            var Q55;
            {var subQ0=sQuery(id+"F0.wireOp",EDGE,"E106");var subQ1=sQuery(id+"F0.wireOp",EDGE,"E105");var subQ2=makeQuery(id+"F0.imprint","INTERSECT",VERTEX,{"derivedFrom":[sQuery(id+"F0.wireOp",EDGE,"E102"),subQ1,subQ0]});Q55=makeQuery(id+"F0.imprint","IMPRINT",FACE,{"disambiguationData":[TD([[makeQuery(id+"F0.imprint","IMPRINT",EDGE,{"disambiguationData":[TD([[subQ2,1.0]])],"derivedFrom":subQ1}),1.0]])]});}
            var Q56;
            {var subQ0=sQuery(id+"F0.wireOp",EDGE,"E114");var subQ1=sQuery(id+"F0.wireOp",EDGE,"E113");var subQ2=makeQuery(id+"F0.imprint","INTERSECT",VERTEX,{"derivedFrom":[sQuery(id+"F0.wireOp",EDGE,"E110"),subQ1,subQ0]});Q56=makeQuery(id+"F0.imprint","IMPRINT",FACE,{"disambiguationData":[TD([[makeQuery(id+"F0.imprint","IMPRINT",EDGE,{"disambiguationData":[TD([[subQ2,1.0]])],"derivedFrom":subQ1}),1.0]])]});}
            var Q57;
            {var subQ0=sQuery(id+"F0.wireOp",EDGE,"E122");var subQ1=sQuery(id+"F0.wireOp",EDGE,"E121");var subQ2=makeQuery(id+"F0.imprint","INTERSECT",VERTEX,{"derivedFrom":[sQuery(id+"F0.wireOp",EDGE,"E118"),subQ1,subQ0]});Q57=makeQuery(id+"F0.imprint","IMPRINT",FACE,{"disambiguationData":[TD([[makeQuery(id+"F0.imprint","IMPRINT",EDGE,{"disambiguationData":[TD([[subQ2,1.0]])],"derivedFrom":subQ1}),1.0]])]});}
            var Q58;
            {var subQ0=sQuery(id+"F0.wireOp",EDGE,"E130");var subQ1=sQuery(id+"F0.wireOp",EDGE,"E129");var subQ2=makeQuery(id+"F0.imprint","INTERSECT",VERTEX,{"derivedFrom":[sQuery(id+"F0.wireOp",EDGE,"E126"),subQ1,subQ0]});Q58=makeQuery(id+"F0.imprint","IMPRINT",FACE,{"disambiguationData":[TD([[makeQuery(id+"F0.imprint","IMPRINT",EDGE,{"disambiguationData":[TD([[subQ2,1.0]])],"derivedFrom":subQ1}),1.0]])]});}
            var Q59;
            {var subQ1=sQuery(id+"F0.wireOp",EDGE,"E141");var subQ3=sQuery(id+"F0.wireOp",EDGE,"E148");var subQ4=makeQuery(id+"F0.imprint","INTERSECT",VERTEX,{"derivedFrom":[subQ1,sQuery(id+"F0.wireOp",EDGE,"E147"),subQ3]});Q59=makeQuery(id+"F0.imprint","IMPRINT",FACE,{"disambiguationData":[TD([[makeQuery(id+"F0.imprint","IMPRINT",EDGE,{"disambiguationData":[TD([[subQ4,-1.0]])],"derivedFrom":subQ3}),-1.0]])]});}
            var Q60;
            {var subQ0=sQuery(id+"F0.wireOp",EDGE,"E1");var subQ1=sQuery(id+"F0.wireOp",EDGE,"E0.bottom");var subQ2=makeQuery(id+"F0.imprint","INTERSECT",VERTEX,{"derivedFrom":[subQ1,sQuery(id+"F0.wireOp",EDGE,"E0.left"),subQ0]});Q60=makeQuery(id+"F0.imprint","IMPRINT",FACE,{"disambiguationData":[TD([[makeQuery(id+"F0.imprint","IMPRINT",EDGE,{"disambiguationData":[TD([[subQ2,-1.0]])],"derivedFrom":subQ1}),-1.0]])]});}
            var Q61;
            {var subQ0=sQuery(id+"F0.wireOp",EDGE,"E9");var subQ1=sQuery(id+"F0.wireOp",EDGE,"E8");var subQ2=makeQuery(id+"F0.imprint","INTERSECT",VERTEX,{"derivedFrom":[sQuery(id+"F0.wireOp",EDGE,"E5"),subQ1,subQ0]});Q61=makeQuery(id+"F0.imprint","IMPRINT",FACE,{"disambiguationData":[TD([[makeQuery(id+"F0.imprint","IMPRINT",EDGE,{"disambiguationData":[TD([[subQ2,1.0]])],"derivedFrom":subQ1}),1.0]])]});}
            var Q62;
            {var subQ0=sQuery(id+"F0.wireOp",EDGE,"E17");var subQ1=sQuery(id+"F0.wireOp",EDGE,"E16");var subQ2=makeQuery(id+"F0.imprint","INTERSECT",VERTEX,{"derivedFrom":[sQuery(id+"F0.wireOp",EDGE,"E13"),subQ1,subQ0]});Q62=makeQuery(id+"F0.imprint","IMPRINT",FACE,{"disambiguationData":[TD([[makeQuery(id+"F0.imprint","IMPRINT",EDGE,{"disambiguationData":[TD([[subQ2,1.0]])],"derivedFrom":subQ1}),1.0]])]});}
            var Q63;
            {var subQ0=sQuery(id+"F0.wireOp",EDGE,"E25");var subQ1=sQuery(id+"F0.wireOp",EDGE,"E24");var subQ2=makeQuery(id+"F0.imprint","INTERSECT",VERTEX,{"derivedFrom":[sQuery(id+"F0.wireOp",EDGE,"E21"),subQ1,subQ0]});Q63=makeQuery(id+"F0.imprint","IMPRINT",FACE,{"disambiguationData":[TD([[makeQuery(id+"F0.imprint","IMPRINT",EDGE,{"disambiguationData":[TD([[subQ2,1.0]])],"derivedFrom":subQ1}),1.0]])]});}
            var Q64;
            {var subQ0=sQuery(id+"F0.wireOp",EDGE,"E33");var subQ1=sQuery(id+"F0.wireOp",EDGE,"E32");var subQ2=makeQuery(id+"F0.imprint","INTERSECT",VERTEX,{"derivedFrom":[sQuery(id+"F0.wireOp",EDGE,"E29"),subQ1,subQ0]});Q64=makeQuery(id+"F0.imprint","IMPRINT",FACE,{"disambiguationData":[TD([[makeQuery(id+"F0.imprint","IMPRINT",EDGE,{"disambiguationData":[TD([[subQ2,1.0]])],"derivedFrom":subQ1}),1.0]])]});}
            var Q65;
            {var subQ0=sQuery(id+"F0.wireOp",EDGE,"E41");var subQ1=sQuery(id+"F0.wireOp",EDGE,"E40");var subQ2=makeQuery(id+"F0.imprint","INTERSECT",VERTEX,{"derivedFrom":[sQuery(id+"F0.wireOp",EDGE,"E37"),subQ1,subQ0]});Q65=makeQuery(id+"F0.imprint","IMPRINT",FACE,{"disambiguationData":[TD([[makeQuery(id+"F0.imprint","IMPRINT",EDGE,{"disambiguationData":[TD([[subQ2,1.0]])],"derivedFrom":subQ1}),1.0]])]});}
            var Q66;
            {var subQ0=sQuery(id+"F0.wireOp",EDGE,"E49");var subQ1=sQuery(id+"F0.wireOp",EDGE,"E48");var subQ2=makeQuery(id+"F0.imprint","INTERSECT",VERTEX,{"derivedFrom":[sQuery(id+"F0.wireOp",EDGE,"E45"),subQ1,subQ0]});Q66=makeQuery(id+"F0.imprint","IMPRINT",FACE,{"disambiguationData":[TD([[makeQuery(id+"F0.imprint","IMPRINT",EDGE,{"disambiguationData":[TD([[subQ2,1.0]])],"derivedFrom":subQ1}),1.0]])]});}
            var Q67;
            {var subQ0=sQuery(id+"F0.wireOp",EDGE,"E57");var subQ1=sQuery(id+"F0.wireOp",EDGE,"E56");var subQ2=makeQuery(id+"F0.imprint","INTERSECT",VERTEX,{"derivedFrom":[sQuery(id+"F0.wireOp",EDGE,"E53"),subQ1,subQ0]});Q67=makeQuery(id+"F0.imprint","IMPRINT",FACE,{"disambiguationData":[TD([[makeQuery(id+"F0.imprint","IMPRINT",EDGE,{"disambiguationData":[TD([[subQ2,1.0]])],"derivedFrom":subQ1}),1.0]])]});}
            var Q68;
            {var subQ0=sQuery(id+"F0.wireOp",EDGE,"E65");var subQ1=sQuery(id+"F0.wireOp",EDGE,"E64");var subQ2=makeQuery(id+"F0.imprint","INTERSECT",VERTEX,{"derivedFrom":[sQuery(id+"F0.wireOp",EDGE,"E61"),subQ1,subQ0]});Q68=makeQuery(id+"F0.imprint","IMPRINT",FACE,{"disambiguationData":[TD([[makeQuery(id+"F0.imprint","IMPRINT",EDGE,{"disambiguationData":[TD([[subQ2,1.0]])],"derivedFrom":subQ1}),1.0]])]});}
            var Q69;
            {var subQ0=sQuery(id+"F0.wireOp",EDGE,"E73");var subQ1=sQuery(id+"F0.wireOp",EDGE,"E72");var subQ2=makeQuery(id+"F0.imprint","INTERSECT",VERTEX,{"derivedFrom":[sQuery(id+"F0.wireOp",EDGE,"E69"),subQ1,subQ0]});Q69=makeQuery(id+"F0.imprint","IMPRINT",FACE,{"disambiguationData":[TD([[makeQuery(id+"F0.imprint","IMPRINT",EDGE,{"disambiguationData":[TD([[subQ2,1.0]])],"derivedFrom":subQ1}),1.0]])]});}
            var Q70;
            {var subQ3=sQuery(id+"F0.wireOp",EDGE,"E84");Q70=makeQuery(id+"F0.imprint","IMPRINT",FACE,{"disambiguationData":[TD([[makeQuery(id+"F0.imprint","IMPRINT",EDGE,{"derivedFrom":subQ3}),-1.0]])]});}
            var Q71;
            {var subQ0=sQuery(id+"F0.wireOp",EDGE,"E87");var subQ1=sQuery(id+"F0.wireOp",EDGE,"E86");var subQ2=makeQuery(id+"F0.imprint","INTERSECT",VERTEX,{"derivedFrom":[sQuery(id+"F0.wireOp",EDGE,"E85"),subQ1,subQ0]});Q71=makeQuery(id+"F0.imprint","IMPRINT",FACE,{"disambiguationData":[TD([[makeQuery(id+"F0.imprint","IMPRINT",EDGE,{"disambiguationData":[TD([[subQ2,1.0]])],"derivedFrom":subQ1}),1.0]])]});}
            var Q72;
            {var subQ0=sQuery(id+"F0.wireOp",EDGE,"E95");var subQ1=sQuery(id+"F0.wireOp",EDGE,"E94");var subQ2=makeQuery(id+"F0.imprint","INTERSECT",VERTEX,{"derivedFrom":[sQuery(id+"F0.wireOp",EDGE,"E91"),subQ1,subQ0]});Q72=makeQuery(id+"F0.imprint","IMPRINT",FACE,{"disambiguationData":[TD([[makeQuery(id+"F0.imprint","IMPRINT",EDGE,{"disambiguationData":[TD([[subQ2,1.0]])],"derivedFrom":subQ1}),1.0]])]});}
            var Q73;
            {var subQ0=sQuery(id+"F0.wireOp",EDGE,"E103");var subQ1=sQuery(id+"F0.wireOp",EDGE,"E102");var subQ2=makeQuery(id+"F0.imprint","INTERSECT",VERTEX,{"derivedFrom":[sQuery(id+"F0.wireOp",EDGE,"E99"),subQ1,subQ0]});Q73=makeQuery(id+"F0.imprint","IMPRINT",FACE,{"disambiguationData":[TD([[makeQuery(id+"F0.imprint","IMPRINT",EDGE,{"disambiguationData":[TD([[subQ2,1.0]])],"derivedFrom":subQ1}),1.0]])]});}
            var Q74;
            {var subQ0=sQuery(id+"F0.wireOp",EDGE,"E111");var subQ1=sQuery(id+"F0.wireOp",EDGE,"E110");var subQ2=makeQuery(id+"F0.imprint","INTERSECT",VERTEX,{"derivedFrom":[sQuery(id+"F0.wireOp",EDGE,"E107"),subQ1,subQ0]});Q74=makeQuery(id+"F0.imprint","IMPRINT",FACE,{"disambiguationData":[TD([[makeQuery(id+"F0.imprint","IMPRINT",EDGE,{"disambiguationData":[TD([[subQ2,1.0]])],"derivedFrom":subQ1}),1.0]])]});}
            var Q75;
            {var subQ0=sQuery(id+"F0.wireOp",EDGE,"E119");var subQ1=sQuery(id+"F0.wireOp",EDGE,"E118");var subQ2=makeQuery(id+"F0.imprint","INTERSECT",VERTEX,{"derivedFrom":[sQuery(id+"F0.wireOp",EDGE,"E115"),subQ1,subQ0]});Q75=makeQuery(id+"F0.imprint","IMPRINT",FACE,{"disambiguationData":[TD([[makeQuery(id+"F0.imprint","IMPRINT",EDGE,{"disambiguationData":[TD([[subQ2,1.0]])],"derivedFrom":subQ1}),1.0]])]});}
            var Q76;
            {var subQ0=sQuery(id+"F0.wireOp",EDGE,"E127");var subQ1=sQuery(id+"F0.wireOp",EDGE,"E126");var subQ2=makeQuery(id+"F0.imprint","INTERSECT",VERTEX,{"derivedFrom":[sQuery(id+"F0.wireOp",EDGE,"E123"),subQ1,subQ0]});Q76=makeQuery(id+"F0.imprint","IMPRINT",FACE,{"disambiguationData":[TD([[makeQuery(id+"F0.imprint","IMPRINT",EDGE,{"disambiguationData":[TD([[subQ2,1.0]])],"derivedFrom":subQ1}),1.0]])]});}
            var Q77;
            {var subQ0=sQuery(id+"F0.wireOp",EDGE,"E135");var subQ1=sQuery(id+"F0.wireOp",EDGE,"E134");var subQ2=makeQuery(id+"F0.imprint","INTERSECT",VERTEX,{"derivedFrom":[sQuery(id+"F0.wireOp",EDGE,"E131"),subQ1,subQ0]});Q77=makeQuery(id+"F0.imprint","IMPRINT",FACE,{"disambiguationData":[TD([[makeQuery(id+"F0.imprint","IMPRINT",EDGE,{"disambiguationData":[TD([[subQ2,1.0]])],"derivedFrom":subQ1}),1.0]])]});}
            var Q78;
            {var subQ0=sQuery(id+"F0.wireOp",EDGE,"E142");Q78=makeQuery(id+"F0.imprint","IMPRINT",FACE,{"disambiguationData":[TD([[makeQuery(id+"F0.imprint","IMPRINT",EDGE,{"derivedFrom":subQ0}),1.0]])]});}
            var Q79;
            {var subQ0=sQuery(id+"F0.wireOp",EDGE,"E150");var subQ1=sQuery(id+"F0.wireOp",EDGE,"E149");var subQ2=makeQuery(id+"F0.imprint","INTERSECT",VERTEX,{"derivedFrom":[sQuery(id+"F0.wireOp",EDGE,"E146"),subQ1,subQ0]});Q79=makeQuery(id+"F0.imprint","IMPRINT",FACE,{"disambiguationData":[TD([[makeQuery(id+"F0.imprint","IMPRINT",EDGE,{"disambiguationData":[TD([[subQ2,1.0]])],"derivedFrom":subQ1}),1.0]])]});}
            extrude(context, id + "F1", {"entities" : qUnion([Q0, Q1, Q2, Q3, Q4, Q5, Q6, Q7, Q8, Q9, Q10, Q11, Q12, Q13, Q14, Q15, Q16, Q17, Q18, Q19, Q20, Q21, Q22, Q23, Q24, Q25, Q26, Q27, Q28, Q29, Q30, Q31, Q32, Q33, Q34, Q35, Q36, Q37, Q38, Q39, Q40, Q41, Q42, Q43, Q44, Q45, Q46, Q47, Q48, Q49, Q50, Q51, Q52, Q53, Q54, Q55, Q56, Q57, Q58, Q59, Q60, Q61, Q62, Q63, Q64, Q65, Q66, Q67, Q68, Q69, Q70, Q71, Q72, Q73, Q74, Q75, Q76, Q77, Q78, Q79]), "depth" : 254 * mm, "offsetDistance" : 25.4 * mm});
        }
        {
            var Q0;
            Q0=makeQuery(id+"F1.opExtrude","SWEPT_FACE",FACE,{"disambiguationData":[OSD([sQuery(id+"F0.wireOp",EDGE,"E0.left")])]});
            var sketch = newSketch(context, id + "F2", { "sketchPlane" : qUnion([Q0])});
            skLineSegment(sketch, "E163", {"start": v(-107.95, 28.93) * mm, "end": v(107.95, 28.93) * mm});
            skLineSegment(sketch, "E164", {"start": v(107.95, 28.93) * mm, "end": v(0, 215.9) * mm});
            skLineSegment(sketch, "E165", {"start": v(0, 215.9) * mm, "end": v(-107.95, 28.93) * mm});
            skLineSegment(sketch, "E166", {"start": v(0, 215.9) * mm, "end": v(-100.2, 28.93) * mm});
            skLineSegment(sketch, "E167", {"start": v(-100.2, 28.93) * mm, "end": v(103.38, 36.85) * mm});
            skLineSegment(sketch, "E168", {"start": v(103.38, 36.85) * mm, "end": v(-3.78, 208.85) * mm});
            skLineSegment(sketch, "E169", {"start": v(-3.78, 208.85) * mm, "end": v(-90.7, 29.3) * mm});
            skLineSegment(sketch, "E170", {"start": v(-90.7, 29.3) * mm, "end": v(99.07, 43.76) * mm});
            skLineSegment(sketch, "E171", {"start": v(99.07, 43.76) * mm, "end": v(-8.05, 200.03) * mm});
            skLineSegment(sketch, "E172", {"start": v(-8.05, 200.03) * mm, "end": v(-80.64, 30.06) * mm});
            skLineSegment(sketch, "E173", {"start": v(-80.64, 30.06) * mm, "end": v(94.04, 51.1) * mm});
            skLineSegment(sketch, "E174", {"start": v(94.04, 51.1) * mm, "end": v(-12.34, 190) * mm});
            skLineSegment(sketch, "E175", {"start": v(-12.34, 190) * mm, "end": v(-69.77, 31.37) * mm});
            skLineSegment(sketch, "E176", {"start": v(-69.77, 31.37) * mm, "end": v(88.22, 58.7) * mm});
            skLineSegment(sketch, "E177", {"start": v(88.22, 58.7) * mm, "end": v(-16, 179.87) * mm});
            skLineSegment(sketch, "E178", {"start": v(-16, 179.87) * mm, "end": v(-59.1, 33.22) * mm});
            skLineSegment(sketch, "E179", {"start": v(-59.1, 33.22) * mm, "end": v(82.1, 65.81) * mm});
            skLineSegment(sketch, "E180", {"start": v(82.1, 65.81) * mm, "end": v(-18.9, 170) * mm});
            skLineSegment(sketch, "E181", {"start": v(-18.9, 170) * mm, "end": v(-50.06, 35.3) * mm});
            skLineSegment(sketch, "E182", {"start": v(-50.06, 35.3) * mm, "end": v(74.97, 73.17) * mm});
            skLineSegment(sketch, "E183", {"start": v(74.97, 73.17) * mm, "end": v(-21.1, 160.5) * mm});
            skLineSegment(sketch, "E184", {"start": v(-21.1, 160.5) * mm, "end": v(-40.54, 38.18) * mm});
            skLineSegment(sketch, "E185", {"start": v(-40.54, 38.18) * mm, "end": v(68.12, 79.4) * mm});
            skLineSegment(sketch, "E186", {"start": v(68.12, 79.4) * mm, "end": v(-22.63, 150.85) * mm});
            skLineSegment(sketch, "E187", {"start": v(-22.63, 150.85) * mm, "end": v(-31.57, 41.59) * mm});
            skLineSegment(sketch, "E188", {"start": v(-31.57, 41.59) * mm, "end": v(61.18, 84.86) * mm});
            skLineSegment(sketch, "E189", {"start": v(61.18, 84.86) * mm, "end": v(-23.36, 141.94) * mm});
            skLineSegment(sketch, "E190", {"start": v(-23.36, 141.94) * mm, "end": v(-23.36, 45.42) * mm});
            skLineSegment(sketch, "E191", {"start": v(-23.36, 45.42) * mm, "end": v(53.7, 89.9) * mm});
            skLineSegment(sketch, "E192", {"start": v(53.7, 89.9) * mm, "end": v(-23.36, 134.4) * mm});
            skLineSegment(sketch, "E193", {"start": v(-23.36, 134.4) * mm, "end": v(-15.15, 50.16) * mm});
            skLineSegment(sketch, "E194", {"start": v(-15.15, 50.16) * mm, "end": v(46.03, 94.34) * mm});
            skLineSegment(sketch, "E195", {"start": v(46.03, 94.34) * mm, "end": v(-22.47, 125.24) * mm});
            skLineSegment(sketch, "E196", {"start": v(-22.47, 125.24) * mm, "end": v(-7.55, 55.64) * mm});
            skLineSegment(sketch, "E197", {"start": v(-7.55, 55.64) * mm, "end": v(35.98, 98.87) * mm});
            skLineSegment(sketch, "E198", {"start": v(35.98, 98.87) * mm, "end": v(-20.4, 115.61) * mm});
            skLineSegment(sketch, "E199", {"start": v(-20.4, 115.61) * mm, "end": v(0, 63.14) * mm});
            skLineSegment(sketch, "E200", {"start": v(0, 63.14) * mm, "end": v(27.16, 101.49) * mm});
            skLineSegment(sketch, "E201", {"start": v(27.16, 101.49) * mm, "end": v(-17.08, 107.07) * mm});
            skLineSegment(sketch, "E202", {"start": v(-17.08, 107.07) * mm, "end": v(5.6, 71.06) * mm});
            skLineSegment(sketch, "E203", {"start": v(5.6, 71.06) * mm, "end": v(17.55, 102.7) * mm});
            skLineSegment(sketch, "E204", {"start": v(17.55, 102.7) * mm, "end": v(-12.48, 99.77) * mm});
            skLineSegment(sketch, "E205", {"start": v(-12.48, 99.77) * mm, "end": v(8.48, 78.66) * mm});
            skLineSegment(sketch, "E206", {"start": v(8.48, 78.66) * mm, "end": v(10.39, 102) * mm});
            skLineSegment(sketch, "E207", {"start": v(10.39, 102) * mm, "end": v(-7.71, 94.96) * mm});
            skLineSegment(sketch, "E208", {"start": v(-7.71, 94.96) * mm, "end": v(8.85, 83.23) * mm});
            skLineSegment(sketch, "E209", {"start": v(8.85, 83.23) * mm, "end": v(7.14, 100.74) * mm});
            skLineSegment(sketch, "E210", {"start": v(7.14, 100.74) * mm, "end": v(-4.85, 92.94) * mm});
            skLineSegment(sketch, "E211", {"start": v(-4.85, 92.94) * mm, "end": v(8.47, 87.16) * mm});
            skLineSegment(sketch, "E212", {"start": v(8.47, 87.16) * mm, "end": v(3.99, 98.69) * mm});
            skLineSegment(sketch, "E213", {"start": v(3.99, 98.69) * mm, "end": v(-1.9, 91.66) * mm});
            skLineSegment(sketch, "E214", {"start": v(-1.9, 91.66) * mm, "end": v(6.52, 90.7) * mm});
            skLineSegment(sketch, "E215", {"start": v(6.52, 90.7) * mm, "end": v(3.03, 97.55) * mm});
            skSolve(sketch);
        }
        {
            var Q0;
            {var subQ0=sQuery(id+"F2.wireOp",EDGE,"E166");var subQ1=sQuery(id+"F2.wireOp",EDGE,"E164");var subQ2=makeQuery(id+"F2.imprint","INTERSECT",VERTEX,{"derivedFrom":[subQ1,sQuery(id+"F2.wireOp",EDGE,"E165"),subQ0]});Q0=makeQuery(id+"F2.imprint","IMPRINT",FACE,{"disambiguationData":[TD([[makeQuery(id+"F2.imprint","IMPRINT",EDGE,{"disambiguationData":[TD([[subQ2,1.0]])],"derivedFrom":subQ1}),1.0]])]});}
            var Q1;
            {var subQ0=sQuery(id+"F2.wireOp",EDGE,"E172");var subQ1=sQuery(id+"F2.wireOp",EDGE,"E171");var subQ2=makeQuery(id+"F2.imprint","INTERSECT",VERTEX,{"derivedFrom":[sQuery(id+"F2.wireOp",EDGE,"E169"),subQ1,subQ0]});Q1=makeQuery(id+"F2.imprint","IMPRINT",FACE,{"disambiguationData":[TD([[makeQuery(id+"F2.imprint","IMPRINT",EDGE,{"disambiguationData":[TD([[subQ2,1.0]])],"derivedFrom":subQ1}),1.0]])]});}
            var Q2;
            {var subQ0=sQuery(id+"F2.wireOp",EDGE,"E178");var subQ1=sQuery(id+"F2.wireOp",EDGE,"E177");var subQ2=makeQuery(id+"F2.imprint","INTERSECT",VERTEX,{"derivedFrom":[sQuery(id+"F2.wireOp",EDGE,"E175"),subQ1,subQ0]});Q2=makeQuery(id+"F2.imprint","IMPRINT",FACE,{"disambiguationData":[TD([[makeQuery(id+"F2.imprint","IMPRINT",EDGE,{"disambiguationData":[TD([[subQ2,1.0]])],"derivedFrom":subQ1}),1.0]])]});}
            var Q3;
            {var subQ0=sQuery(id+"F2.wireOp",EDGE,"E184");var subQ1=sQuery(id+"F2.wireOp",EDGE,"E183");var subQ2=makeQuery(id+"F2.imprint","INTERSECT",VERTEX,{"derivedFrom":[sQuery(id+"F2.wireOp",EDGE,"E181"),subQ1,subQ0]});Q3=makeQuery(id+"F2.imprint","IMPRINT",FACE,{"disambiguationData":[TD([[makeQuery(id+"F2.imprint","IMPRINT",EDGE,{"disambiguationData":[TD([[subQ2,1.0]])],"derivedFrom":subQ1}),1.0]])]});}
            var Q4;
            {var subQ0=sQuery(id+"F2.wireOp",EDGE,"E190");var subQ1=sQuery(id+"F2.wireOp",EDGE,"E189");var subQ2=makeQuery(id+"F2.imprint","INTERSECT",VERTEX,{"derivedFrom":[sQuery(id+"F2.wireOp",EDGE,"E187"),subQ1,subQ0]});Q4=makeQuery(id+"F2.imprint","IMPRINT",FACE,{"disambiguationData":[TD([[makeQuery(id+"F2.imprint","IMPRINT",EDGE,{"disambiguationData":[TD([[subQ2,1.0]])],"derivedFrom":subQ1}),1.0]])]});}
            var Q5;
            {var subQ0=sQuery(id+"F2.wireOp",EDGE,"E196");var subQ1=sQuery(id+"F2.wireOp",EDGE,"E195");var subQ2=makeQuery(id+"F2.imprint","INTERSECT",VERTEX,{"derivedFrom":[sQuery(id+"F2.wireOp",EDGE,"E193"),subQ1,subQ0]});Q5=makeQuery(id+"F2.imprint","IMPRINT",FACE,{"disambiguationData":[TD([[makeQuery(id+"F2.imprint","IMPRINT",EDGE,{"disambiguationData":[TD([[subQ2,1.0]])],"derivedFrom":subQ1}),1.0]])]});}
            var Q6;
            {var subQ0=sQuery(id+"F2.wireOp",EDGE,"E202");var subQ1=sQuery(id+"F2.wireOp",EDGE,"E201");var subQ2=makeQuery(id+"F2.imprint","INTERSECT",VERTEX,{"derivedFrom":[sQuery(id+"F2.wireOp",EDGE,"E199"),subQ1,subQ0]});Q6=makeQuery(id+"F2.imprint","IMPRINT",FACE,{"disambiguationData":[TD([[makeQuery(id+"F2.imprint","IMPRINT",EDGE,{"disambiguationData":[TD([[subQ2,1.0]])],"derivedFrom":subQ1}),1.0]])]});}
            var Q7;
            {var subQ0=sQuery(id+"F2.wireOp",EDGE,"E208");var subQ1=sQuery(id+"F2.wireOp",EDGE,"E207");var subQ2=makeQuery(id+"F2.imprint","INTERSECT",VERTEX,{"derivedFrom":[sQuery(id+"F2.wireOp",EDGE,"E205"),subQ1,subQ0]});Q7=makeQuery(id+"F2.imprint","IMPRINT",FACE,{"disambiguationData":[TD([[makeQuery(id+"F2.imprint","IMPRINT",EDGE,{"disambiguationData":[TD([[subQ2,1.0]])],"derivedFrom":subQ1}),1.0]])]});}
            var Q8;
            {var subQ0=sQuery(id+"F2.wireOp",EDGE,"E214");Q8=makeQuery(id+"F2.imprint","IMPRINT",FACE,{"disambiguationData":[TD([[makeQuery(id+"F2.imprint","IMPRINT",EDGE,{"derivedFrom":subQ0}),1.0]])]});}
            var Q9;
            {var subQ0=sQuery(id+"F2.wireOp",EDGE,"E165");Q9=makeQuery(id+"F2.imprint","IMPRINT",FACE,{"disambiguationData":[TD([[makeQuery(id+"F2.imprint","IMPRINT",EDGE,{"derivedFrom":subQ0}),1.0]])]});}
            var Q10;
            {var subQ0=sQuery(id+"F2.wireOp",EDGE,"E170");var subQ1=sQuery(id+"F2.wireOp",EDGE,"E169");var subQ2=makeQuery(id+"F2.imprint","INTERSECT",VERTEX,{"derivedFrom":[sQuery(id+"F2.wireOp",EDGE,"E167"),subQ1,subQ0]});Q10=makeQuery(id+"F2.imprint","IMPRINT",FACE,{"disambiguationData":[TD([[makeQuery(id+"F2.imprint","IMPRINT",EDGE,{"disambiguationData":[TD([[subQ2,1.0]])],"derivedFrom":subQ1}),1.0]])]});}
            var Q11;
            {var subQ0=sQuery(id+"F2.wireOp",EDGE,"E176");var subQ1=sQuery(id+"F2.wireOp",EDGE,"E175");var subQ2=makeQuery(id+"F2.imprint","INTERSECT",VERTEX,{"derivedFrom":[sQuery(id+"F2.wireOp",EDGE,"E173"),subQ1,subQ0]});Q11=makeQuery(id+"F2.imprint","IMPRINT",FACE,{"disambiguationData":[TD([[makeQuery(id+"F2.imprint","IMPRINT",EDGE,{"disambiguationData":[TD([[subQ2,1.0]])],"derivedFrom":subQ1}),1.0]])]});}
            var Q12;
            {var subQ0=sQuery(id+"F2.wireOp",EDGE,"E182");var subQ1=sQuery(id+"F2.wireOp",EDGE,"E181");var subQ2=makeQuery(id+"F2.imprint","INTERSECT",VERTEX,{"derivedFrom":[sQuery(id+"F2.wireOp",EDGE,"E179"),subQ1,subQ0]});Q12=makeQuery(id+"F2.imprint","IMPRINT",FACE,{"disambiguationData":[TD([[makeQuery(id+"F2.imprint","IMPRINT",EDGE,{"disambiguationData":[TD([[subQ2,1.0]])],"derivedFrom":subQ1}),1.0]])]});}
            var Q13;
            {var subQ0=sQuery(id+"F2.wireOp",EDGE,"E188");var subQ1=sQuery(id+"F2.wireOp",EDGE,"E187");var subQ2=makeQuery(id+"F2.imprint","INTERSECT",VERTEX,{"derivedFrom":[sQuery(id+"F2.wireOp",EDGE,"E185"),subQ1,subQ0]});Q13=makeQuery(id+"F2.imprint","IMPRINT",FACE,{"disambiguationData":[TD([[makeQuery(id+"F2.imprint","IMPRINT",EDGE,{"disambiguationData":[TD([[subQ2,1.0]])],"derivedFrom":subQ1}),1.0]])]});}
            var Q14;
            {var subQ0=sQuery(id+"F2.wireOp",EDGE,"E194");var subQ1=sQuery(id+"F2.wireOp",EDGE,"E193");var subQ2=makeQuery(id+"F2.imprint","INTERSECT",VERTEX,{"derivedFrom":[sQuery(id+"F2.wireOp",EDGE,"E191"),subQ1,subQ0]});Q14=makeQuery(id+"F2.imprint","IMPRINT",FACE,{"disambiguationData":[TD([[makeQuery(id+"F2.imprint","IMPRINT",EDGE,{"disambiguationData":[TD([[subQ2,1.0]])],"derivedFrom":subQ1}),1.0]])]});}
            var Q15;
            {var subQ0=sQuery(id+"F2.wireOp",EDGE,"E200");var subQ1=sQuery(id+"F2.wireOp",EDGE,"E199");var subQ2=makeQuery(id+"F2.imprint","INTERSECT",VERTEX,{"derivedFrom":[sQuery(id+"F2.wireOp",EDGE,"E197"),subQ1,subQ0]});Q15=makeQuery(id+"F2.imprint","IMPRINT",FACE,{"disambiguationData":[TD([[makeQuery(id+"F2.imprint","IMPRINT",EDGE,{"disambiguationData":[TD([[subQ2,1.0]])],"derivedFrom":subQ1}),1.0]])]});}
            var Q16;
            {var subQ0=sQuery(id+"F2.wireOp",EDGE,"E206");var subQ1=sQuery(id+"F2.wireOp",EDGE,"E205");var subQ2=makeQuery(id+"F2.imprint","INTERSECT",VERTEX,{"derivedFrom":[sQuery(id+"F2.wireOp",EDGE,"E203"),subQ1,subQ0]});Q16=makeQuery(id+"F2.imprint","IMPRINT",FACE,{"disambiguationData":[TD([[makeQuery(id+"F2.imprint","IMPRINT",EDGE,{"disambiguationData":[TD([[subQ2,1.0]])],"derivedFrom":subQ1}),1.0]])]});}
            var Q17;
            {var subQ3=sQuery(id+"F2.wireOp",EDGE,"E212");Q17=makeQuery(id+"F2.imprint","IMPRINT",FACE,{"disambiguationData":[TD([[makeQuery(id+"F2.imprint","IMPRINT",EDGE,{"derivedFrom":subQ3}),-1.0]])]});}
            var Q18;
            {var subQ0=sQuery(id+"F2.wireOp",EDGE,"E204");var subQ1=sQuery(id+"F2.wireOp",EDGE,"E203");var subQ2=makeQuery(id+"F2.imprint","INTERSECT",VERTEX,{"derivedFrom":[sQuery(id+"F2.wireOp",EDGE,"E201"),subQ1,subQ0]});Q18=makeQuery(id+"F2.imprint","IMPRINT",FACE,{"disambiguationData":[TD([[makeQuery(id+"F2.imprint","IMPRINT",EDGE,{"disambiguationData":[TD([[subQ2,1.0]])],"derivedFrom":subQ1}),1.0]])]});}
            var Q19;
            {var subQ0=sQuery(id+"F2.wireOp",EDGE,"E198");var subQ1=sQuery(id+"F2.wireOp",EDGE,"E197");var subQ2=makeQuery(id+"F2.imprint","INTERSECT",VERTEX,{"derivedFrom":[sQuery(id+"F2.wireOp",EDGE,"E195"),subQ1,subQ0]});Q19=makeQuery(id+"F2.imprint","IMPRINT",FACE,{"disambiguationData":[TD([[makeQuery(id+"F2.imprint","IMPRINT",EDGE,{"disambiguationData":[TD([[subQ2,1.0]])],"derivedFrom":subQ1}),1.0]])]});}
            var Q20;
            {var subQ0=sQuery(id+"F2.wireOp",EDGE,"E192");var subQ1=sQuery(id+"F2.wireOp",EDGE,"E191");var subQ2=makeQuery(id+"F2.imprint","INTERSECT",VERTEX,{"derivedFrom":[sQuery(id+"F2.wireOp",EDGE,"E189"),subQ1,subQ0]});Q20=makeQuery(id+"F2.imprint","IMPRINT",FACE,{"disambiguationData":[TD([[makeQuery(id+"F2.imprint","IMPRINT",EDGE,{"disambiguationData":[TD([[subQ2,1.0]])],"derivedFrom":subQ1}),1.0]])]});}
            var Q21;
            {var subQ0=sQuery(id+"F2.wireOp",EDGE,"E186");var subQ1=sQuery(id+"F2.wireOp",EDGE,"E185");var subQ2=makeQuery(id+"F2.imprint","INTERSECT",VERTEX,{"derivedFrom":[sQuery(id+"F2.wireOp",EDGE,"E183"),subQ1,subQ0]});Q21=makeQuery(id+"F2.imprint","IMPRINT",FACE,{"disambiguationData":[TD([[makeQuery(id+"F2.imprint","IMPRINT",EDGE,{"disambiguationData":[TD([[subQ2,1.0]])],"derivedFrom":subQ1}),1.0]])]});}
            var Q22;
            {var subQ0=sQuery(id+"F2.wireOp",EDGE,"E180");var subQ1=sQuery(id+"F2.wireOp",EDGE,"E179");var subQ2=makeQuery(id+"F2.imprint","INTERSECT",VERTEX,{"derivedFrom":[sQuery(id+"F2.wireOp",EDGE,"E177"),subQ1,subQ0]});Q22=makeQuery(id+"F2.imprint","IMPRINT",FACE,{"disambiguationData":[TD([[makeQuery(id+"F2.imprint","IMPRINT",EDGE,{"disambiguationData":[TD([[subQ2,1.0]])],"derivedFrom":subQ1}),1.0]])]});}
            var Q23;
            {var subQ0=sQuery(id+"F2.wireOp",EDGE,"E174");var subQ1=sQuery(id+"F2.wireOp",EDGE,"E173");var subQ2=makeQuery(id+"F2.imprint","INTERSECT",VERTEX,{"derivedFrom":[sQuery(id+"F2.wireOp",EDGE,"E171"),subQ1,subQ0]});Q23=makeQuery(id+"F2.imprint","IMPRINT",FACE,{"disambiguationData":[TD([[makeQuery(id+"F2.imprint","IMPRINT",EDGE,{"disambiguationData":[TD([[subQ2,1.0]])],"derivedFrom":subQ1}),1.0]])]});}
            var Q24;
            {var subQ0=sQuery(id+"F2.wireOp",EDGE,"E168");var subQ1=sQuery(id+"F2.wireOp",EDGE,"E167");var subQ2=makeQuery(id+"F2.imprint","INTERSECT",VERTEX,{"derivedFrom":[sQuery(id+"F2.wireOp",EDGE,"E164"),subQ1,subQ0]});Q24=makeQuery(id+"F2.imprint","IMPRINT",FACE,{"disambiguationData":[TD([[makeQuery(id+"F2.imprint","IMPRINT",EDGE,{"disambiguationData":[TD([[subQ2,1.0]])],"derivedFrom":subQ1}),1.0]])]});}
            extrude(context, id + "F3", {"entities" : qUnion([Q0, Q1, Q2, Q3, Q4, Q5, Q6, Q7, Q8, Q9, Q10, Q11, Q12, Q13, Q14, Q15, Q16, Q17, Q18, Q19, Q20, Q21, Q22, Q23, Q24]), "operationType" : NewBodyOperationType.REMOVE, "endBound" : BoundingType.THROUGH_ALL, "oppositeDirection" : true, "depth" : 25.4 * mm, "offsetDistance" : 25.4 * mm});
        }
    });
